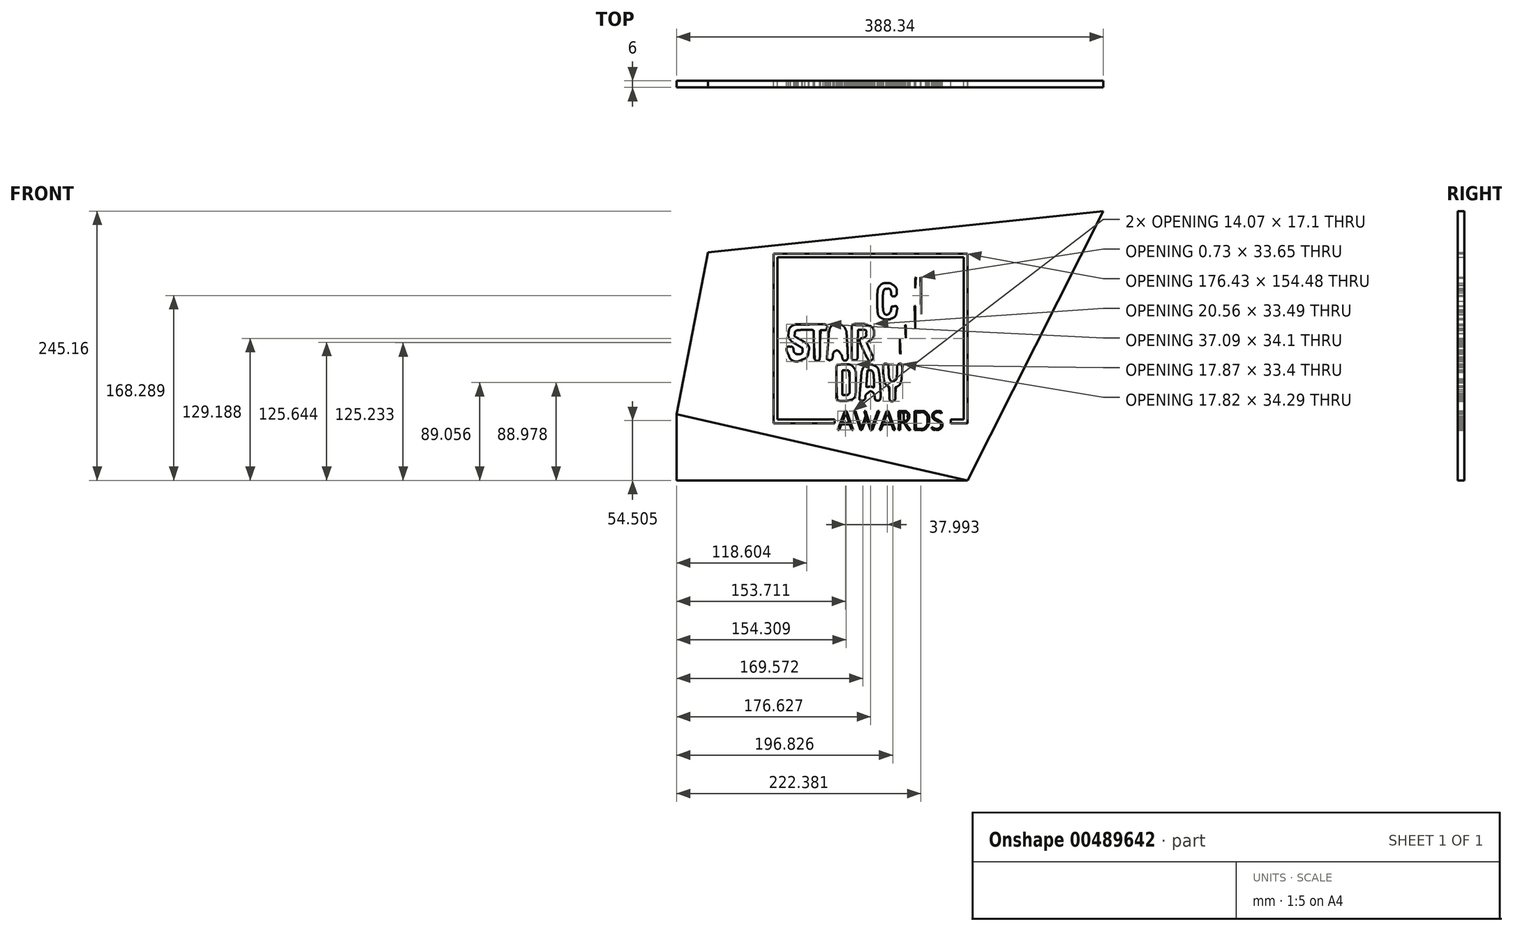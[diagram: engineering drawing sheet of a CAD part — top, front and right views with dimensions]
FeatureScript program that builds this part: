
annotation { "Feature Type Name" : "Feature", "Feature Type Description" : "" }
export const myFeature = defineFeature(function(context is Context, id is Id, definition is map)
    precondition{}
    {
        {
            var Q0;
            Q0=qCreatedBy(makeId("Front.planeOp"),FACE);
            var sketch = newSketch(context, id + "F0", { "sketchPlane" : qUnion([Q0])});
            skLineSegment(sketch, "E0", {"start": v(194.17, 122.58) * mm, "end": v(-165.67, 84.87) * mm});
            skLineSegment(sketch, "E1", {"start": v(-165.67, 84.87) * mm, "end": v(-194.17, -62.37) * mm});
            skLineSegment(sketch, "E2", {"start": v(-194.17, -62.37) * mm, "end": v(70.56, -122.58) * mm});
            skLineSegment(sketch, "E3", {"start": v(70.56, -122.58) * mm, "end": v(194.17, 122.58) * mm});
            skFitSpline(sketch, "E4", {"points": [v(25.61, 63.48) * mm, v(26.39, 63.52) * mm, v(27.2, 63.2) * mm, v(27.85, 62.53) * mm]});
            skLineSegment(sketch, "E5", {"start": v(-105.76, 83.85) * mm, "end": v(70.67, 83.85) * mm});
            skLineSegment(sketch, "E6", {"start": v(70.67, 83.85) * mm, "end": v(70.67, -70.63) * mm});
            skLineSegment(sketch, "E7", {"start": v(70.67, -70.63) * mm, "end": v(55.35, -70.63) * mm});
            skLineSegment(sketch, "E8", {"start": v(55.35, -70.63) * mm, "end": v(55.35, -67.25) * mm});
            skLineSegment(sketch, "E9", {"start": v(55.35, -67.25) * mm, "end": v(67.29, -67.25) * mm});
            skLineSegment(sketch, "E10", {"start": v(67.29, -67.25) * mm, "end": v(67.29, 80.46) * mm});
            skLineSegment(sketch, "E11", {"start": v(67.29, 80.46) * mm, "end": v(-102.37, 80.46) * mm});
            skLineSegment(sketch, "E12", {"start": v(-102.37, 80.46) * mm, "end": v(-102.37, -67.25) * mm});
            skLineSegment(sketch, "E13", {"start": v(-102.37, -67.25) * mm, "end": v(-50.2, -67.25) * mm});
            skLineSegment(sketch, "E14", {"start": v(-50.2, -67.25) * mm, "end": v(-50.2, -70.63) * mm});
            skLineSegment(sketch, "E15", {"start": v(-50.2, -70.63) * mm, "end": v(-105.76, -70.63) * mm});
            skLineSegment(sketch, "E16", {"start": v(-105.76, -70.63) * mm, "end": v(-105.76, 82.16) * mm});
            skLineSegment(sketch, "E17", {"start": v(-105.76, 82.16) * mm, "end": v(-105.76, 83.85) * mm});
            skFitSpline(sketch, "E18", {"points": [v(28.58, 28.89) * mm, v(28.61, 7.58) * mm, v(28.55, -4.5) * mm, v(28.4, -5.32) * mm]});
            skFitSpline(sketch, "E19", {"points": [v(28.4, -5.32) * mm, v(27.66, -9.33) * mm, v(24.53, -12.47) * mm, v(20.51, -13.23) * mm]});
            skLineSegment(sketch, "E20", {"start": v(27.85, 62.53) * mm, "end": v(28.52, 61.83) * mm});
            skLineSegment(sketch, "E21", {"start": v(28.52, 61.83) * mm, "end": v(28.58, 28.89) * mm});
            skLineSegment(sketch, "E22", {"start": v(28.58, 28.89) * mm, "end": v(27.85, 62.53) * mm});
            skFitSpline(sketch, "E23", {"points": [v(20.51, -13.23) * mm, v(16.18, -14.05) * mm, v(11.76, -11.73) * mm, v(9.83, -7.6) * mm]});
            skLineSegment(sketch, "E24", {"start": v(20.51, -13.23) * mm, "end": v(20.51, -13.23) * mm});
            skFitSpline(sketch, "E25", {"points": [v(8.98, 5.9) * mm, v(8.91, 19.23) * mm, v(8.87, 18.91) * mm, v(10.63, 19.77) * mm]});
            skFitSpline(sketch, "E26", {"points": [v(10.63, 19.77) * mm, v(11.38, 20.14) * mm, v(11.66, 20.16) * mm, v(12.39, 19.95) * mm]});
            skFitSpline(sketch, "E27", {"points": [v(12.39, 19.95) * mm, v(12.86, 19.8) * mm, v(13.5, 19.42) * mm, v(13.81, 19.09) * mm]});
            skLineSegment(sketch, "E28", {"start": v(9.83, -7.6) * mm, "end": v(9.05, -5.93) * mm});
            skLineSegment(sketch, "E29", {"start": v(9.05, -5.93) * mm, "end": v(8.98, 5.9) * mm});
            skLineSegment(sketch, "E30", {"start": v(8.98, 5.9) * mm, "end": v(9.83, -7.6) * mm});
            skFitSpline(sketch, "E31", {"points": [v(14.5, 6.86) * mm, v(14.62, -6.1) * mm, v(14.56, -5.6) * mm, v(16.25, -6.88) * mm]});
            skFitSpline(sketch, "E32", {"points": [v(16.25, -6.88) * mm, v(17.12, -7.55) * mm, v(18.97, -7.87) * mm, v(20.17, -7.57) * mm]});
            skFitSpline(sketch, "E33", {"points": [v(20.17, -7.57) * mm, v(21.1, -7.34) * mm, v(22.57, -5.87) * mm, v(22.83, -4.92) * mm]});
            skFitSpline(sketch, "E34", {"points": [v(22.83, -4.92) * mm, v(22.98, -4.38) * mm, v(23.07, 3.16) * mm, v(23.07, 16.04) * mm]});
            skLineSegment(sketch, "E35", {"start": v(13.81, 19.09) * mm, "end": v(14.38, 18.49) * mm});
            skLineSegment(sketch, "E36", {"start": v(14.38, 18.49) * mm, "end": v(14.5, 6.86) * mm});
            skLineSegment(sketch, "E37", {"start": v(14.5, 6.86) * mm, "end": v(13.81, 19.09) * mm});
            skFitSpline(sketch, "E38", {"points": [v(22.47, 36.37) * mm, v(21.71, 36.66) * mm, v(15.42, 36.66) * mm, v(14.96, 36.37) * mm]});
            skFitSpline(sketch, "E39", {"points": [v(14.96, 36.37) * mm, v(14.67, 36.2) * mm, v(14.59, 35.18) * mm, v(14.5, 30.49) * mm]});
            skFitSpline(sketch, "E40", {"points": [v(14.5, 30.49) * mm, v(14.38, 24.9) * mm, v(14.37, 24.8) * mm, v(13.82, 24.23) * mm]});
            skFitSpline(sketch, "E41", {"points": [v(13.82, 24.23) * mm, v(13, 23.36) * mm, v(11.98, 23.08) * mm, v(10.9, 23.44) * mm]});
            skFitSpline(sketch, "E42", {"points": [v(10.9, 23.44) * mm, v(9.08, 24.05) * mm, v(9.19, 23.16) * mm, v(9.01, 39.2) * mm]});
            skFitSpline(sketch, "E43", {"points": [v(9.01, 39.2) * mm, v(8.87, 52.48) * mm, v(8.88, 53.56) * mm, v(9.26, 54.55) * mm]});
            skFitSpline(sketch, "E44", {"points": [v(9.26, 54.55) * mm, v(9.72, 55.74) * mm, v(10.52, 56.3) * mm, v(11.76, 56.3) * mm]});
            skFitSpline(sketch, "E45", {"points": [v(11.76, 56.3) * mm, v(12.76, 56.3) * mm, v(13.89, 55.6) * mm, v(14.21, 54.76) * mm]});
            skFitSpline(sketch, "E46", {"points": [v(14.21, 54.76) * mm, v(14.36, 54.38) * mm, v(14.55, 51.58) * mm, v(14.66, 48.19) * mm]});
            skLineSegment(sketch, "E47", {"start": v(23.07, 16.04) * mm, "end": v(23.07, 36.15) * mm});
            skLineSegment(sketch, "E48", {"start": v(23.07, 36.15) * mm, "end": v(22.47, 36.37) * mm});
            skLineSegment(sketch, "E49", {"start": v(22.47, 36.37) * mm, "end": v(23.07, 16.04) * mm});
            skFitSpline(sketch, "E50", {"points": [v(18.71, 42.22) * mm, v(22.24, 42.16) * mm, v(22.6, 42.19) * mm, v(22.8, 42.57) * mm]});
            skFitSpline(sketch, "E51", {"points": [v(22.8, 42.57) * mm, v(22.94, 42.81) * mm, v(23.03, 46.77) * mm, v(23.03, 52.21) * mm]});
            skLineSegment(sketch, "E52", {"start": v(14.66, 48.19) * mm, "end": v(14.84, 42.28) * mm});
            skLineSegment(sketch, "E53", {"start": v(14.84, 42.28) * mm, "end": v(18.71, 42.22) * mm});
            skLineSegment(sketch, "E54", {"start": v(18.71, 42.22) * mm, "end": v(14.66, 48.19) * mm});
            skFitSpline(sketch, "E55", {"points": [v(23.63, 62.34) * mm, v(24.1, 63.06) * mm, v(24.84, 63.45) * mm, v(25.61, 63.48) * mm]});
            skLineSegment(sketch, "E56", {"start": v(23.03, 52.21) * mm, "end": v(23.04, 61.44) * mm});
            skLineSegment(sketch, "E57", {"start": v(23.04, 61.44) * mm, "end": v(23.63, 62.34) * mm});
            skLineSegment(sketch, "E58", {"start": v(23.63, 62.34) * mm, "end": v(23.03, 52.21) * mm});
            skLineSegment(sketch, "E59", {"start": v(25.61, 63.48) * mm, "end": v(25.61, 63.48) * mm});
            skFitSpline(sketch, "E60", {"points": [v(-44, 57.23) * mm, v(-34.34, 57.23) * mm, v(-34.33, 57.23) * mm, v(-33.6, 55.7) * mm]});
            skFitSpline(sketch, "E61", {"points": [v(-33.6, 55.7) * mm, v(-33.16, 54.77) * mm, v(-33.16, 54.41) * mm, v(-33.59, 53.39) * mm]});
            skFitSpline(sketch, "E62", {"points": [v(-33.59, 53.39) * mm, v(-34.12, 52.11) * mm, v(-35.35, 51.68) * mm, v(-38.4, 51.67) * mm]});
            skFitSpline(sketch, "E63", {"points": [v(-38.4, 51.67) * mm, v(-40.52, 51.67) * mm, v(-40.91, 51.6) * mm, v(-41.1, 51.26) * mm]});
            skFitSpline(sketch, "E64", {"points": [v(-41.1, 51.26) * mm, v(-41.22, 51.03) * mm, v(-41.32, 45.5) * mm, v(-41.33, 38.48) * mm]});
            skFitSpline(sketch, "E65", {"points": [v(-41.33, 38.48) * mm, v(-41.35, 25.1) * mm, v(-41.3, 25.51) * mm, v(-42.6, 24.67) * mm]});
            skFitSpline(sketch, "E66", {"points": [v(-42.6, 24.67) * mm, v(-43.45, 24.11) * mm, v(-44.41, 24.04) * mm, v(-45.26, 24.47) * mm]});
            skFitSpline(sketch, "E67", {"points": [v(-45.26, 24.47) * mm, v(-46.87, 25.28) * mm, v(-46.8, 24.7) * mm, v(-46.86, 38.33) * mm]});
            skFitSpline(sketch, "E68", {"points": [v(-46.86, 38.33) * mm, v(-46.9, 45.09) * mm, v(-46.98, 50.86) * mm, v(-47.04, 51.14) * mm]});
            skFitSpline(sketch, "E69", {"points": [v(-47.04, 51.14) * mm, v(-47.16, 51.64) * mm, v(-47.27, 51.67) * mm, v(-49.49, 51.67) * mm]});
            skFitSpline(sketch, "E70", {"points": [v(-49.49, 51.67) * mm, v(-52.1, 51.67) * mm, v(-53.06, 51.95) * mm, v(-53.86, 52.97) * mm]});
            skFitSpline(sketch, "E71", {"points": [v(-53.86, 52.97) * mm, v(-54.64, 53.96) * mm, v(-54.44, 55.68) * mm, v(-53.44, 56.58) * mm]});
            skLineSegment(sketch, "E72", {"start": v(-52.71, 57.23) * mm, "end": v(-44, 57.23) * mm});
            skLineSegment(sketch, "E73", {"start": v(-44, 57.23) * mm, "end": v(-52.71, 57.23) * mm});
            skFitSpline(sketch, "E74", {"points": [v(-21.12, 57.18) * mm, v(-18.97, 57.2) * mm, v(-17.15, 57.15) * mm, v(-16.73, 57.01) * mm]});
            skFitSpline(sketch, "E75", {"points": [v(-16.73, 57.01) * mm, v(-14.36, 56.23) * mm, v(-13.97, 53.27) * mm, v(-16.08, 52.04) * mm]});
            skFitSpline(sketch, "E76", {"points": [v(-16.08, 52.04) * mm, v(-16.78, 51.63) * mm, v(-17.34, 51.57) * mm, v(-20.9, 51.54) * mm]});
            skFitSpline(sketch, "E77", {"points": [v(-20.9, 51.54) * mm, v(-23.12, 51.51) * mm, v(-25.03, 51.4) * mm, v(-25.14, 51.3) * mm]});
            skFitSpline(sketch, "E78", {"points": [v(-25.14, 51.3) * mm, v(-25.47, 50.96) * mm, v(-25.49, 44.97) * mm, v(-25.16, 44.64) * mm]});
            skFitSpline(sketch, "E79", {"points": [v(-25.16, 44.64) * mm, v(-24.92, 44.4) * mm, v(-21.76, 44.25) * mm, v(-17.06, 44.25) * mm]});
            skFitSpline(sketch, "E80", {"points": [v(-17.06, 44.25) * mm, v(-16.48, 44.25) * mm, v(-16.08, 44.04) * mm, v(-15.47, 43.43) * mm]});
            skFitSpline(sketch, "E81", {"points": [v(-15.47, 43.43) * mm, v(-14.7, 42.67) * mm, v(-14.66, 42.54) * mm, v(-14.76, 41.44) * mm]});
            skFitSpline(sketch, "E82", {"points": [v(-14.76, 41.44) * mm, v(-14.9, 40.03) * mm, v(-15.6, 39.22) * mm, v(-16.93, 38.9) * mm]});
            skFitSpline(sketch, "E83", {"points": [v(-16.93, 38.9) * mm, v(-17.43, 38.8) * mm, v(-19.48, 38.7) * mm, v(-21.5, 38.7) * mm]});
            skFitSpline(sketch, "E84", {"points": [v(-21.5, 38.7) * mm, v(-24.76, 38.69) * mm, v(-25.17, 38.64) * mm, v(-25.31, 38.28) * mm]});
            skFitSpline(sketch, "E85", {"points": [v(-25.31, 38.28) * mm, v(-25.52, 37.75) * mm, v(-25.53, 30.58) * mm, v(-25.32, 30.05) * mm]});
            skFitSpline(sketch, "E86", {"points": [v(-25.32, 30.05) * mm, v(-25.17, 29.69) * mm, v(-24.75, 29.65) * mm, v(-21.2, 29.65) * mm]});
            skFitSpline(sketch, "E87", {"points": [v(-21.2, 29.65) * mm, v(-16.85, 29.65) * mm, v(-16.09, 29.48) * mm, v(-15.19, 28.34) * mm]});
            skFitSpline(sketch, "E88", {"points": [v(-15.19, 28.34) * mm, v(-14.76, 27.8) * mm, v(-14.68, 27.47) * mm, v(-14.77, 26.56) * mm]});
            skFitSpline(sketch, "E89", {"points": [v(-14.77, 26.56) * mm, v(-14.93, 24.88) * mm, v(-15.6, 24.32) * mm, v(-17.75, 24.07) * mm]});
            skFitSpline(sketch, "E90", {"points": [v(-17.75, 24.07) * mm, v(-19.9, 23.82) * mm, v(-27.76, 23.84) * mm, v(-28.84, 24.1) * mm]});
            skFitSpline(sketch, "E91", {"points": [v(-28.84, 24.1) * mm, v(-30.04, 24.37) * mm, v(-30.86, 25.42) * mm, v(-31.04, 26.9) * mm]});
            skFitSpline(sketch, "E92", {"points": [v(-31.04, 26.9) * mm, v(-31.13, 27.59) * mm, v(-31.16, 34.2) * mm, v(-31.12, 41.58) * mm]});
            skFitSpline(sketch, "E93", {"points": [v(-31.12, 41.58) * mm, v(-31.04, 56.16) * mm, v(-31.05, 56.08) * mm, v(-29.77, 56.69) * mm]});
            skFitSpline(sketch, "E94", {"points": [v(-29.77, 56.69) * mm, v(-29.22, 56.95) * mm, v(-24.7, 57.16) * mm, v(-21.12, 57.18) * mm]});
            skLineSegment(sketch, "E95", {"start": v(-53.44, 56.58) * mm, "end": v(-52.71, 57.23) * mm});
            skLineSegment(sketch, "E96", {"start": v(-52.71, 57.23) * mm, "end": v(-53.44, 56.58) * mm});
            skFitSpline(sketch, "E97", {"points": [v(-2.88, 57) * mm, v(-0.9, 57.04) * mm, v(1.1, 56.52) * mm, v(2.56, 55.42) * mm]});
            skFitSpline(sketch, "E98", {"points": [v(2.56, 55.42) * mm, v(4.95, 53.61) * mm, v(6.15, 51.23) * mm, v(6.15, 48.3) * mm]});
            skFitSpline(sketch, "E99", {"points": [v(6.15, 48.3) * mm, v(6.15, 46.72) * mm, v(6.1, 46.5) * mm, v(5.47, 45.82) * mm]});
            skFitSpline(sketch, "E100", {"points": [v(5.47, 45.82) * mm, v(4.9, 45.17) * mm, v(4.64, 45.06) * mm, v(3.74, 45.06) * mm]});
            skFitSpline(sketch, "E101", {"points": [v(3.74, 45.06) * mm, v(2.2, 45.06) * mm, v(1.39, 45.94) * mm, v(1.07, 47.92) * mm]});
            skFitSpline(sketch, "E102", {"points": [v(1.07, 47.92) * mm, v(0.65, 50.58) * mm, v(-0.54, 51.76) * mm, v(-2.79, 51.76) * mm]});
            skFitSpline(sketch, "E103", {"points": [v(-2.79, 51.76) * mm, v(-4.16, 51.76) * mm, v(-5.02, 51.3) * mm, v(-5.55, 50.28) * mm]});
            skFitSpline(sketch, "E104", {"points": [v(-5.55, 50.28) * mm, v(-6.08, 49.26) * mm, v(-6.36, 45.87) * mm, v(-6.36, 40.54) * mm]});
            skFitSpline(sketch, "E105", {"points": [v(-6.36, 40.54) * mm, v(-6.35, 35.14) * mm, v(-6.07, 31.58) * mm, v(-5.57, 30.6) * mm]});
            skFitSpline(sketch, "E106", {"points": [v(-5.57, 30.6) * mm, v(-4.55, 28.64) * mm, v(-1.68, 28.5) * mm, v(0, 30.35) * mm]});
            skFitSpline(sketch, "E107", {"points": [v(0, 30.35) * mm, v(0.62, 31.05) * mm, v(0.82, 31.54) * mm, v(1.05, 32.88) * mm]});
            skFitSpline(sketch, "E108", {"points": [v(1.05, 32.88) * mm, v(1.4, 35) * mm, v(1.95, 35.68) * mm, v(3.38, 35.83) * mm]});
            skFitSpline(sketch, "E109", {"points": [v(3.38, 35.83) * mm, v(5.61, 36.05) * mm, v(6.67, 34.44) * mm, v(6.19, 31.53) * mm]});
            skFitSpline(sketch, "E110", {"points": [v(6.19, 31.53) * mm, v(5.68, 28.48) * mm, v(3.82, 25.95) * mm, v(1.17, 24.69) * mm]});
            skFitSpline(sketch, "E111", {"points": [v(1.17, 24.69) * mm, v(0.05, 24.16) * mm, v(-0.61, 24.01) * mm, v(-2.2, 23.95) * mm]});
            skFitSpline(sketch, "E112", {"points": [v(-2.2, 23.95) * mm, v(-4.4, 23.86) * mm, v(-5.4, 24.05) * mm, v(-7, 24.87) * mm]});
            skFitSpline(sketch, "E113", {"points": [v(-7, 24.87) * mm, v(-9, 25.9) * mm, v(-10.82, 28.38) * mm, v(-11.11, 30.5) * mm]});
            skFitSpline(sketch, "E114", {"points": [v(-11.11, 30.5) * mm, v(-11.34, 32.1) * mm, v(-11.4, 48.03) * mm, v(-11.2, 49.58) * mm]});
            skFitSpline(sketch, "E115", {"points": [v(-11.2, 49.58) * mm, v(-10.93, 51.47) * mm, v(-9.93, 53.65) * mm, v(-8.8, 54.79) * mm]});
            skFitSpline(sketch, "E116", {"points": [v(-8.8, 54.79) * mm, v(-7.37, 56.21) * mm, v(-5.13, 56.97) * mm, v(-2.88, 57) * mm]});
            skLineSegment(sketch, "E117", {"start": v(-21.12, 57.18) * mm, "end": v(-21.12, 57.18) * mm});
            skFitSpline(sketch, "E118", {"points": [v(-4.3, 20.06) * mm, v(0.03, 20.07) * mm, v(4.36, 19.96) * mm, v(4.8, 19.72) * mm]});
            skFitSpline(sketch, "E119", {"points": [v(4.8, 19.72) * mm, v(6, 19.08) * mm, v(6.5, 17.24) * mm, v(5.87, 15.85) * mm]});
            skFitSpline(sketch, "E120", {"points": [v(5.87, 15.85) * mm, v(5.4, 14.81) * mm, v(4.46, 14.5) * mm, v(1.4, 14.4) * mm]});
            skFitSpline(sketch, "E121", {"points": [v(1.4, 14.4) * mm, v(-0.3, 14.33) * mm, v(-1.45, 14.2) * mm, v(-1.55, 14.03) * mm]});
            skFitSpline(sketch, "E122", {"points": [v(-1.55, 14.03) * mm, v(-1.65, 13.89) * mm, v(-1.72, 8.21) * mm, v(-1.73, 1.42) * mm]});
            skFitSpline(sketch, "E123", {"points": [v(-1.73, 1.42) * mm, v(-1.73, -11.88) * mm, v(-1.72, -11.78) * mm, v(-2.94, -12.63) * mm]});
            skFitSpline(sketch, "E124", {"points": [v(-2.94, -12.63) * mm, v(-3.73, -13.19) * mm, v(-5.43, -13.1) * mm, v(-6.17, -12.47) * mm]});
            skFitSpline(sketch, "E125", {"points": [v(-6.17, -12.47) * mm, v(-6.5, -12.19) * mm, v(-6.9, -11.73) * mm, v(-7.04, -11.45) * mm]});
            skFitSpline(sketch, "E126", {"points": [v(-7.04, -11.45) * mm, v(-7.21, -11.1) * mm, v(-7.3, -7.02) * mm, v(-7.3, 1.6) * mm]});
            skFitSpline(sketch, "E127", {"points": [v(-7.3, 1.6) * mm, v(-7.3, 12.68) * mm, v(-7.33, 14.15) * mm, v(-7.65, 14.27) * mm]});
            skFitSpline(sketch, "E128", {"points": [v(-7.65, 14.27) * mm, v(-7.85, 14.35) * mm, v(-8.76, 14.43) * mm, v(-9.68, 14.46) * mm]});
            skFitSpline(sketch, "E129", {"points": [v(-9.68, 14.46) * mm, v(-13.17, 14.56) * mm, v(-13.09, 14.54) * mm, v(-13.92, 15.37) * mm]});
            skFitSpline(sketch, "E130", {"points": [v(-13.92, 15.37) * mm, v(-14.56, 16.01) * mm, v(-14.7, 16.34) * mm, v(-14.7, 17.12) * mm]});
            skFitSpline(sketch, "E131", {"points": [v(-14.7, 17.12) * mm, v(-14.7, 18.32) * mm, v(-14.24, 19.25) * mm, v(-13.42, 19.69) * mm]});
            skFitSpline(sketch, "E132", {"points": [v(-13.42, 19.69) * mm, v(-12.97, 19.93) * mm, v(-8.64, 20.06) * mm, v(-4.3, 20.06) * mm]});
            skFitSpline(sketch, "E133", {"points": [v(-28.16, 19.77) * mm, v(-23.87, 19.8) * mm, v(-22.59, 19.59) * mm, v(-20.44, 18.5) * mm]});
            skFitSpline(sketch, "E134", {"points": [v(-20.44, 18.5) * mm, v(-15.48, 15.96) * mm, v(-14.92, 8.12) * mm, v(-19.4, 4.02) * mm]});
            skFitSpline(sketch, "E135", {"points": [v(-19.4, 4.02) * mm, v(-20.08, 3.4) * mm, v(-20.72, 2.75) * mm, v(-20.8, 2.6) * mm]});
            skFitSpline(sketch, "E136", {"points": [v(-20.8, 2.6) * mm, v(-20.9, 2.44) * mm, v(-20.16, 0.53) * mm, v(-19.09, -1.8) * mm]});
            skFitSpline(sketch, "E137", {"points": [v(-19.09, -1.8) * mm, v(-18.05, -4.07) * mm, v(-16.8, -6.8) * mm, v(-16.3, -7.87) * mm]});
            skFitSpline(sketch, "E138", {"points": [v(-16.3, -7.87) * mm, v(-15.2, -10.26) * mm, v(-15.14, -11.3) * mm, v(-16.04, -12.3) * mm]});
            skFitSpline(sketch, "E139", {"points": [v(-16.04, -12.3) * mm, v(-17.13, -13.51) * mm, v(-19.33, -13.36) * mm, v(-20.07, -12.03) * mm]});
            skFitSpline(sketch, "E140", {"points": [v(-20.07, -12.03) * mm, v(-22, -8.55) * mm, v(-27.46, 3.74) * mm, v(-27.46, 4.6) * mm]});
            skFitSpline(sketch, "E141", {"points": [v(-27.46, 4.6) * mm, v(-27.46, 5.65) * mm, v(-26.47, 6.64) * mm, v(-25, 7.07) * mm]});
            skFitSpline(sketch, "E142", {"points": [v(-25, 7.07) * mm, v(-22.8, 7.7) * mm, v(-21.66, 9.12) * mm, v(-21.66, 11.21) * mm]});
            skFitSpline(sketch, "E143", {"points": [v(-21.66, 11.21) * mm, v(-21.66, 13.68) * mm, v(-22.82, 14.44) * mm, v(-26.64, 14.46) * mm]});
            skFitSpline(sketch, "E144", {"points": [v(-29.3, 1.6) * mm, v(-29.4, -8.12) * mm, v(-29.5, -11.38) * mm, v(-29.72, -11.77) * mm]});
            skFitSpline(sketch, "E145", {"points": [v(-29.72, -11.77) * mm, v(-30.2, -12.6) * mm, v(-30.96, -13) * mm, v(-32.12, -13) * mm]});
            skFitSpline(sketch, "E146", {"points": [v(-32.12, -13) * mm, v(-33.64, -13) * mm, v(-34.55, -12.1) * mm, v(-34.75, -10.39) * mm]});
            skFitSpline(sketch, "E147", {"points": [v(-34.75, -10.39) * mm, v(-34.83, -9.72) * mm, v(-34.87, -3.12) * mm, v(-34.83, 4.28) * mm]});
            skFitSpline(sketch, "E148", {"points": [v(-34.83, 4.28) * mm, v(-34.76, 16.85) * mm, v(-34.73, 17.78) * mm, v(-34.33, 18.38) * mm]});
            skFitSpline(sketch, "E149", {"points": [v(-34.33, 18.38) * mm, v(-33.59, 19.52) * mm, v(-32.64, 19.73) * mm, v(-28.16, 19.77) * mm]});
            skLineSegment(sketch, "E150", {"start": v(-26.64, 14.46) * mm, "end": v(-29.2, 14.47) * mm});
            skLineSegment(sketch, "E151", {"start": v(-29.2, 14.47) * mm, "end": v(-29.3, 1.6) * mm});
            skLineSegment(sketch, "E152", {"start": v(-29.3, 1.6) * mm, "end": v(-26.64, 14.46) * mm});
            skFitSpline(sketch, "E153", {"points": [v(-58.5, 19.16) * mm, v(-57.44, 18.45) * mm, v(-57.02, 17.24) * mm, v(-57.42, 16.05) * mm]});
            skFitSpline(sketch, "E154", {"points": [v(-57.42, 16.05) * mm, v(-57.86, 14.72) * mm, v(-58.7, 14.26) * mm, v(-60.78, 14.17) * mm]});
            skFitSpline(sketch, "E155", {"points": [v(-60.78, 14.17) * mm, v(-61.76, 14.13) * mm, v(-62.8, 14.05) * mm, v(-63.09, 13.99) * mm]});
            skLineSegment(sketch, "E156", {"start": v(-59.3, 19.7) * mm, "end": v(-58.5, 19.16) * mm});
            skLineSegment(sketch, "E157", {"start": v(-58.5, 19.16) * mm, "end": v(-59.3, 19.7) * mm});
            skFitSpline(sketch, "E158", {"points": [v(-63.62, 2) * mm, v(-63.62, -4.53) * mm, v(-63.72, -10.29) * mm, v(-63.84, -10.8) * mm]});
            skFitSpline(sketch, "E159", {"points": [v(-63.84, -10.8) * mm, v(-64.32, -12.91) * mm, v(-66.72, -13.73) * mm, v(-68.3, -12.32) * mm]});
            skLineSegment(sketch, "E160", {"start": v(-63.09, 13.99) * mm, "end": v(-63.61, 13.88) * mm});
            skLineSegment(sketch, "E161", {"start": v(-63.61, 13.88) * mm, "end": v(-63.62, 2) * mm});
            skLineSegment(sketch, "E162", {"start": v(-63.62, 2) * mm, "end": v(-63.09, 13.99) * mm});
            skFitSpline(sketch, "E163", {"points": [v(-69.17, 1.01) * mm, v(-69.27, 11.93) * mm, v(-69.34, 13.7) * mm, v(-69.64, 13.9) * mm]});
            skFitSpline(sketch, "E164", {"points": [v(-69.64, 13.9) * mm, v(-70.17, 14.23) * mm, v(-83.7, 14.16) * mm, v(-84.68, 13.82) * mm]});
            skFitSpline(sketch, "E165", {"points": [v(-84.68, 13.82) * mm, v(-85.75, 13.44) * mm, v(-86.37, 12.53) * mm, v(-86.5, 11.13) * mm]});
            skFitSpline(sketch, "E166", {"points": [v(-86.5, 11.13) * mm, v(-86.72, 8.88) * mm, v(-86.13, 8.22) * mm, v(-81.43, 5.53) * mm]});
            skFitSpline(sketch, "E167", {"points": [v(-81.43, 5.53) * mm, v(-79.85, 4.63) * mm, v(-78, 3.47) * mm, v(-77.32, 2.95) * mm]});
            skFitSpline(sketch, "E168", {"points": [v(-77.32, 2.95) * mm, v(-74.75, 1.01) * mm, v(-73.5, -2.07) * mm, v(-74.04, -5.13) * mm]});
            skFitSpline(sketch, "E169", {"points": [v(-74.04, -5.13) * mm, v(-74.7, -8.8) * mm, v(-76.87, -11.5) * mm, v(-80.07, -12.67) * mm]});
            skFitSpline(sketch, "E170", {"points": [v(-80.07, -12.67) * mm, v(-84.92, -14.42) * mm, v(-90.27, -12.3) * mm, v(-92.39, -7.77) * mm]});
            skFitSpline(sketch, "E171", {"points": [v(-92.39, -7.77) * mm, v(-94.1, -4.11) * mm, v(-93.27, -0.94) * mm, v(-90.6, -0.94) * mm]});
            skFitSpline(sketch, "E172", {"points": [v(-90.6, -0.94) * mm, v(-88.9, -0.94) * mm, v(-88.03, -1.98) * mm, v(-87.6, -4.5) * mm]});
            skFitSpline(sketch, "E173", {"points": [v(-87.6, -4.5) * mm, v(-87.43, -5.52) * mm, v(-86.2, -7) * mm, v(-85.16, -7.44) * mm]});
            skFitSpline(sketch, "E174", {"points": [v(-85.16, -7.44) * mm, v(-84.76, -7.6) * mm, v(-83.93, -7.68) * mm, v(-83.21, -7.62) * mm]});
            skFitSpline(sketch, "E175", {"points": [v(-83.21, -7.62) * mm, v(-81.04, -7.44) * mm, v(-79.6, -5.9) * mm, v(-79.6, -3.75) * mm]});
            skFitSpline(sketch, "E176", {"points": [v(-79.6, -3.75) * mm, v(-79.6, -2.42) * mm, v(-80.37, -1.66) * mm, v(-83.63, 0.26) * mm]});
            skFitSpline(sketch, "E177", {"points": [v(-83.63, 0.26) * mm, v(-87.4, 2.47) * mm, v(-89.66, 4.04) * mm, v(-90.33, 4.93) * mm]});
            skFitSpline(sketch, "E178", {"points": [v(-90.33, 4.93) * mm, v(-91.71, 6.74) * mm, v(-92.47, 9.23) * mm, v(-92.22, 11.1) * mm]});
            skFitSpline(sketch, "E179", {"points": [v(-92.22, 11.1) * mm, v(-91.68, 15) * mm, v(-89.99, 17.58) * mm, v(-87.05, 18.96) * mm]});
            skLineSegment(sketch, "E180", {"start": v(-68.3, -12.32) * mm, "end": v(-69.06, -11.64) * mm});
            skLineSegment(sketch, "E181", {"start": v(-69.06, -11.64) * mm, "end": v(-69.17, 1.01) * mm});
            skLineSegment(sketch, "E182", {"start": v(-69.17, 1.01) * mm, "end": v(-68.3, -12.32) * mm});
            skFitSpline(sketch, "E183", {"points": [v(38.27, 19.68) * mm, v(42.97, 19.68) * mm, v(43.83, 19.62) * mm, v(45.13, 19.22) * mm]});
            skFitSpline(sketch, "E184", {"points": [v(45.13, 19.22) * mm, v(51.98, 17.1) * mm, v(54.28, 8.86) * mm, v(49.48, 3.6) * mm]});
            skFitSpline(sketch, "E185", {"points": [v(49.48, 3.6) * mm, v(47.42, 1.35) * mm, v(45.1, 0.45) * mm, v(41.3, 0.45) * mm]});
            skFitSpline(sketch, "E186", {"points": [v(41.3, 0.45) * mm, v(39.93, 0.45) * mm, v(38.6, 0.34) * mm, v(38.35, 0.2) * mm]});
            skFitSpline(sketch, "E187", {"points": [v(38.35, 0.2) * mm, v(37.93, -0.02) * mm, v(37.9, -0.33) * mm, v(37.9, -5.38) * mm]});
            skFitSpline(sketch, "E188", {"points": [v(37.9, -5.38) * mm, v(37.9, -11.1) * mm, v(37.77, -11.88) * mm, v(36.66, -12.66) * mm]});
            skFitSpline(sketch, "E189", {"points": [v(36.66, -12.66) * mm, v(36, -13.12) * mm, v(34.2, -13.08) * mm, v(33.57, -12.59) * mm]});
            skFitSpline(sketch, "E190", {"points": [v(33.57, -12.59) * mm, v(32.34, -11.63) * mm, v(32.34, -11.64) * mm, v(32.34, 4.33) * mm]});
            skFitSpline(sketch, "E191", {"points": [v(32.34, 4.33) * mm, v(32.34, 15.53) * mm, v(32.4, 19.2) * mm, v(32.62, 19.4) * mm]});
            skFitSpline(sketch, "E192", {"points": [v(32.62, 19.4) * mm, v(32.82, 19.6) * mm, v(34.4, 19.68) * mm, v(38.27, 19.68) * mm]});
            skLineSegment(sketch, "E193", {"start": v(-87.05, 18.96) * mm, "end": v(-85.74, 19.57) * mm});
            skLineSegment(sketch, "E194", {"start": v(-85.74, 19.57) * mm, "end": v(-72.53, 19.63) * mm});
            skLineSegment(sketch, "E195", {"start": v(-72.53, 19.63) * mm, "end": v(-59.3, 19.7) * mm});
            skLineSegment(sketch, "E196", {"start": v(-59.3, 19.7) * mm, "end": v(-87.05, 18.96) * mm});
            skFitSpline(sketch, "E197", {"points": [v(-47.75, 19.59) * mm, v(-46.55, 19.6) * mm, v(-45.35, 19.42) * mm, v(-44.56, 19.05) * mm]});
            skFitSpline(sketch, "E198", {"points": [v(-44.56, 19.05) * mm, v(-42.93, 18.31) * mm, v(-41.23, 16.6) * mm, v(-40.41, 14.88) * mm]});
            skFitSpline(sketch, "E199", {"points": [v(-40.41, 14.88) * mm, v(-39.56, 13.1) * mm, v(-39.47, 12.25) * mm, v(-38.81, 0.62) * mm]});
            skFitSpline(sketch, "E200", {"points": [v(-38.81, 0.62) * mm, v(-38.2, -10.18) * mm, v(-38.2, -11.37) * mm, v(-38.82, -12.15) * mm]});
            skFitSpline(sketch, "E201", {"points": [v(-38.82, -12.15) * mm, v(-39.75, -13.33) * mm, v(-42.11, -13.38) * mm, v(-42.86, -12.23) * mm]});
            skFitSpline(sketch, "E202", {"points": [v(-42.86, -12.23) * mm, v(-43.04, -11.95) * mm, v(-43.36, -10.95) * mm, v(-43.57, -10.02) * mm]});
            skFitSpline(sketch, "E203", {"points": [v(-43.57, -10.02) * mm, v(-43.9, -8.54) * mm, v(-44.1, -8.16) * mm, v(-45.04, -7.2) * mm]});
            skFitSpline(sketch, "E204", {"points": [v(-45.04, -7.2) * mm, v(-47.76, -4.39) * mm, v(-51.12, -5.7) * mm, v(-52, -9.94) * mm]});
            skFitSpline(sketch, "E205", {"points": [v(-52, -9.94) * mm, v(-52.36, -11.68) * mm, v(-52.86, -12.52) * mm, v(-53.77, -12.9) * mm]});
            skFitSpline(sketch, "E206", {"points": [v(-53.77, -12.9) * mm, v(-54.73, -13.3) * mm, v(-54.95, -13.3) * mm, v(-55.91, -12.88) * mm]});
            skFitSpline(sketch, "E207", {"points": [v(-55.91, -12.88) * mm, v(-57.36, -12.25) * mm, v(-57.42, -11.72) * mm, v(-56.9, -5.06) * mm]});
            skFitSpline(sketch, "E208", {"points": [v(-56.9, -5.06) * mm, v(-55.67, 10.46) * mm, v(-55.46, 12.7) * mm, v(-55.13, 13.89) * mm]});
            skFitSpline(sketch, "E209", {"points": [v(-55.13, 13.89) * mm, v(-54.43, 16.37) * mm, v(-53.04, 18.1) * mm, v(-50.98, 19.03) * mm]});
            skFitSpline(sketch, "E210", {"points": [v(-50.98, 19.03) * mm, v(-50.17, 19.4) * mm, v(-48.96, 19.58) * mm, v(-47.75, 19.59) * mm]});
            skFitSpline(sketch, "E211", {"points": [v(-47.88, 14.39) * mm, v(-48.67, 14.37) * mm, v(-49.41, 13.98) * mm, v(-49.81, 13.2) * mm]});
            skFitSpline(sketch, "E212", {"points": [v(-49.81, 13.2) * mm, v(-50.26, 12.35) * mm, v(-50.69, 8.24) * mm, v(-51.15, 0.45) * mm]});
            skFitSpline(sketch, "E213", {"points": [v(-51.15, 0.45) * mm, v(-51.22, -0.71) * mm, v(-51.24, -0.7) * mm, v(-48.84, -0.57) * mm]});
            skFitSpline(sketch, "E214", {"points": [v(-48.84, -0.57) * mm, v(-47.22, -0.48) * mm, v(-46.28, -0.54) * mm, v(-45.53, -0.78) * mm]});
            skFitSpline(sketch, "E215", {"points": [v(-45.53, -0.78) * mm, v(-44.71, -1.04) * mm, v(-44.44, -1.05) * mm, v(-44.26, -0.83) * mm]});
            skFitSpline(sketch, "E216", {"points": [v(-44.26, -0.83) * mm, v(-43.82, -0.3) * mm, v(-44.64, 11.68) * mm, v(-45.19, 12.74) * mm]});
            skFitSpline(sketch, "E217", {"points": [v(-45.19, 12.74) * mm, v(-45.76, 13.84) * mm, v(-46.86, 14.42) * mm, v(-47.88, 14.39) * mm]});
            skFitSpline(sketch, "E218", {"points": [v(39.95, 14.1) * mm, v(38.95, 14.1) * mm, v(38.43, 14.04) * mm, v(38.25, 13.89) * mm]});
            skFitSpline(sketch, "E219", {"points": [v(38.25, 13.89) * mm, v(37.97, 13.65) * mm, v(37.9, 12.92) * mm, v(37.9, 10.1) * mm]});
            skFitSpline(sketch, "E220", {"points": [v(37.9, 10.1) * mm, v(37.9, 8.16) * mm, v(37.99, 6.47) * mm, v(38.08, 6.32) * mm]});
            skFitSpline(sketch, "E221", {"points": [v(38.08, 6.32) * mm, v(38.17, 6.18) * mm, v(38.46, 6) * mm, v(38.71, 5.94) * mm]});
            skFitSpline(sketch, "E222", {"points": [v(38.71, 5.94) * mm, v(39.4, 5.77) * mm, v(43, 6) * mm, v(43.83, 6.25) * mm]});
            skFitSpline(sketch, "E223", {"points": [v(43.83, 6.25) * mm, v(45.16, 6.68) * mm, v(46.48, 8.6) * mm, v(46.48, 10.1) * mm]});
            skFitSpline(sketch, "E224", {"points": [v(46.48, 10.1) * mm, v(46.48, 11.16) * mm, v(45.57, 12.7) * mm, v(44.56, 13.38) * mm]});
            skFitSpline(sketch, "E225", {"points": [v(44.56, 13.38) * mm, v(43.72, 13.94) * mm, v(43.37, 14) * mm, v(41.1, 14.09) * mm]});
            skFitSpline(sketch, "E226", {"points": [v(41.1, 14.09) * mm, v(40.66, 14.1) * mm, v(40.28, 14.1) * mm, v(39.95, 14.1) * mm]});
            skFitSpline(sketch, "E227", {"points": [v(9.31, -16.4) * mm, v(9.94, -16.41) * mm, v(10.58, -16.62) * mm, v(10.98, -17.02) * mm]});
            skFitSpline(sketch, "E228", {"points": [v(11.29, -21.76) * mm, v(10.91, -27.37) * mm, v(10.37, -31.63) * mm, v(9.85, -33.13) * mm]});
            skFitSpline(sketch, "E229", {"points": [v(9.85, -33.13) * mm, v(9.15, -35.1) * mm, v(8, -36.35) * mm, v(5.7, -37.61) * mm]});
            skLineSegment(sketch, "E230", {"start": v(10.98, -17.02) * mm, "end": v(11.57, -17.62) * mm});
            skLineSegment(sketch, "E231", {"start": v(11.57, -17.62) * mm, "end": v(11.29, -21.76) * mm});
            skLineSegment(sketch, "E232", {"start": v(11.29, -21.76) * mm, "end": v(10.98, -17.02) * mm});
            skFitSpline(sketch, "E233", {"points": [v(5, -43.17) * mm, v(4.99, -47.93) * mm, v(4.95, -48.4) * mm, v(4.53, -49.1) * mm]});
            skFitSpline(sketch, "E234", {"points": [v(4.53, -49.1) * mm, v(4.27, -49.52) * mm, v(3.8, -49.96) * mm, v(3.47, -50.08) * mm]});
            skFitSpline(sketch, "E235", {"points": [v(3.47, -50.08) * mm, v(1.93, -50.67) * mm, v(0.16, -50) * mm, v(-0.3, -48.68) * mm]});
            skFitSpline(sketch, "E236", {"points": [v(-0.3, -48.68) * mm, v(-0.47, -48.2) * mm, v(-0.57, -46.02) * mm, v(-0.57, -42.84) * mm]});
            skLineSegment(sketch, "E237", {"start": v(5.7, -37.61) * mm, "end": v(5, -38) * mm});
            skLineSegment(sketch, "E238", {"start": v(5, -38) * mm, "end": v(5, -43.17) * mm});
            skLineSegment(sketch, "E239", {"start": v(5, -43.17) * mm, "end": v(5.7, -37.61) * mm});
            skFitSpline(sketch, "E240", {"points": [v(-1.18, -37.26) * mm, v(-4.05, -34.88) * mm, v(-5.02, -33.39) * mm, v(-5.44, -30.67) * mm]});
            skFitSpline(sketch, "E241", {"points": [v(-5.44, -30.67) * mm, v(-5.81, -28.23) * mm, v(-6.19, -18.27) * mm, v(-5.93, -17.59) * mm]});
            skFitSpline(sketch, "E242", {"points": [v(-5.93, -17.59) * mm, v(-5.62, -16.78) * mm, v(-5.02, -16.47) * mm, v(-3.7, -16.47) * mm]});
            skFitSpline(sketch, "E243", {"points": [v(-3.7, -16.47) * mm, v(-2.89, -16.47) * mm, v(-2.5, -16.6) * mm, v(-2.09, -17.02) * mm]});
            skFitSpline(sketch, "E244", {"points": [v(-2.09, -17.02) * mm, v(-1.42, -17.69) * mm, v(-1.36, -18.15) * mm, v(-1.09, -24.16) * mm]});
            skFitSpline(sketch, "E245", {"points": [v(-1.09, -24.16) * mm, v(-0.89, -28.54) * mm, v(-0.85, -28.78) * mm, v(-0.2, -30.06) * mm]});
            skFitSpline(sketch, "E246", {"points": [v(-0.2, -30.06) * mm, v(0.64, -31.74) * mm, v(1.4, -32.31) * mm, v(2.78, -32.31) * mm]});
            skFitSpline(sketch, "E247", {"points": [v(2.78, -32.31) * mm, v(3.58, -32.31) * mm, v(3.98, -32.17) * mm, v(4.44, -31.75) * mm]});
            skFitSpline(sketch, "E248", {"points": [v(4.44, -31.75) * mm, v(5.86, -30.42) * mm, v(6.24, -28.75) * mm, v(6.5, -22.61) * mm]});
            skFitSpline(sketch, "E249", {"points": [v(6.5, -22.61) * mm, v(6.66, -18.63) * mm, v(6.85, -17.7) * mm, v(7.63, -16.96) * mm]});
            skFitSpline(sketch, "E250", {"points": [v(7.63, -16.96) * mm, v(8.04, -16.57) * mm, v(8.68, -16.39) * mm, v(9.31, -16.4) * mm]});
            skLineSegment(sketch, "E251", {"start": v(-0.57, -42.84) * mm, "end": v(-0.57, -37.76) * mm});
            skLineSegment(sketch, "E252", {"start": v(-0.57, -37.76) * mm, "end": v(-1.18, -37.26) * mm});
            skLineSegment(sketch, "E253", {"start": v(-1.18, -37.26) * mm, "end": v(-0.57, -42.84) * mm});
            skFitSpline(sketch, "E254", {"points": [v(-41.57, -17) * mm, v(-37.32, -16.98) * mm, v(-34.97, -17.8) * mm, v(-33.04, -19.83) * mm]});
            skFitSpline(sketch, "E255", {"points": [v(-33.04, -19.83) * mm, v(-32.16, -20.76) * mm, v(-31.79, -21.4) * mm, v(-31.42, -22.6) * mm]});
            skFitSpline(sketch, "E256", {"points": [v(-31.42, -22.6) * mm, v(-30.96, -24.08) * mm, v(-30.93, -24.7) * mm, v(-30.93, -33.26) * mm]});
            skFitSpline(sketch, "E257", {"points": [v(-30.93, -33.26) * mm, v(-30.93, -39.17) * mm, v(-31.02, -42.82) * mm, v(-31.2, -43.68) * mm]});
            skFitSpline(sketch, "E258", {"points": [v(-31.2, -43.68) * mm, v(-31.74, -46.4) * mm, v(-33.79, -48.62) * mm, v(-36.58, -49.52) * mm]});
            skFitSpline(sketch, "E259", {"points": [v(-36.58, -49.52) * mm, v(-37.97, -49.96) * mm, v(-45.64, -50.2) * mm, v(-46.82, -49.84) * mm]});
            skFitSpline(sketch, "E260", {"points": [v(-46.82, -49.84) * mm, v(-47.2, -49.72) * mm, v(-47.78, -49.35) * mm, v(-48.1, -49.02) * mm]});
            skFitSpline(sketch, "E261", {"points": [v(-48.72, -33.87) * mm, v(-48.77, -24.6) * mm, v(-48.7, -19.1) * mm, v(-48.56, -18.7) * mm]});
            skFitSpline(sketch, "E262", {"points": [v(-48.56, -18.7) * mm, v(-48.11, -17.53) * mm, v(-47.2, -17.23) * mm, v(-43.51, -17.05) * mm]});
            skFitSpline(sketch, "E263", {"points": [v(-43.51, -17.05) * mm, v(-42.82, -17.01) * mm, v(-42.18, -17) * mm, v(-41.57, -17) * mm]});
            skLineSegment(sketch, "E264", {"start": v(-48.1, -49.02) * mm, "end": v(-48.66, -48.42) * mm});
            skLineSegment(sketch, "E265", {"start": v(-48.66, -48.42) * mm, "end": v(-48.72, -33.87) * mm});
            skLineSegment(sketch, "E266", {"start": v(-48.72, -33.87) * mm, "end": v(-48.1, -49.02) * mm});
            skFitSpline(sketch, "E267", {"points": [v(-18.18, -17.29) * mm, v(-16.29, -17.28) * mm, v(-15.8, -17.37) * mm, v(-14.67, -17.9) * mm]});
            skFitSpline(sketch, "E268", {"points": [v(-14.67, -17.9) * mm, v(-12.34, -19) * mm, v(-10.64, -21.22) * mm, v(-10.1, -23.89) * mm]});
            skFitSpline(sketch, "E269", {"points": [v(-10.1, -23.89) * mm, v(-9.66, -26.08) * mm, v(-8.5, -47.03) * mm, v(-8.77, -48.08) * mm]});
            skFitSpline(sketch, "E270", {"points": [v(-8.77, -48.08) * mm, v(-9.04, -49.15) * mm, v(-9.92, -49.85) * mm, v(-11, -49.85) * mm]});
            skFitSpline(sketch, "E271", {"points": [v(-11, -49.85) * mm, v(-12.1, -49.85) * mm, v(-13.19, -49.36) * mm, v(-13.43, -48.75) * mm]});
            skFitSpline(sketch, "E272", {"points": [v(-13.43, -48.75) * mm, v(-13.52, -48.53) * mm, v(-13.74, -47.69) * mm, v(-13.91, -46.89) * mm]});
            skFitSpline(sketch, "E273", {"points": [v(-13.91, -46.89) * mm, v(-14.69, -43.27) * mm, v(-17.68, -41.5) * mm, v(-20.2, -43.17) * mm]});
            skFitSpline(sketch, "E274", {"points": [v(-20.2, -43.17) * mm, v(-21.2, -43.84) * mm, v(-22.36, -45.77) * mm, v(-22.36, -46.8) * mm]});
            skFitSpline(sketch, "E275", {"points": [v(-22.36, -46.8) * mm, v(-22.36, -47.82) * mm, v(-23.24, -49.31) * mm, v(-24.08, -49.7) * mm]});
            skFitSpline(sketch, "E276", {"points": [v(-24.08, -49.7) * mm, v(-25.02, -50.15) * mm, v(-25.27, -50.16) * mm, v(-26.22, -49.74) * mm]});
            skFitSpline(sketch, "E277", {"points": [v(-26.22, -49.74) * mm, v(-27.39, -49.23) * mm, v(-27.77, -48.23) * mm, v(-27.6, -46.15) * mm]});
            skFitSpline(sketch, "E278", {"points": [v(-27.6, -46.15) * mm, v(-25.97, -25.52) * mm, v(-25.78, -23.7) * mm, v(-25.12, -21.93) * mm]});
            skFitSpline(sketch, "E279", {"points": [v(-25.12, -21.93) * mm, v(-24.53, -20.34) * mm, v(-23.08, -18.7) * mm, v(-21.57, -17.91) * mm]});
            skFitSpline(sketch, "E280", {"points": [v(-21.57, -17.91) * mm, v(-20.53, -17.36) * mm, v(-20.13, -17.29) * mm, v(-18.18, -17.29) * mm]});
            skFitSpline(sketch, "E281", {"points": [v(-41.49, -22.28) * mm, v(-42.41, -22.29) * mm, v(-42.93, -22.36) * mm, v(-43.1, -22.5) * mm]});
            skFitSpline(sketch, "E282", {"points": [v(-43.1, -22.5) * mm, v(-43.4, -22.75) * mm, v(-43.45, -24.38) * mm, v(-43.45, -33.61) * mm]});
            skFitSpline(sketch, "E283", {"points": [v(-43.45, -33.61) * mm, v(-43.45, -39.57) * mm, v(-43.38, -44.5) * mm, v(-43.3, -44.6) * mm]});
            skFitSpline(sketch, "E284", {"points": [v(-43.3, -44.6) * mm, v(-43.2, -44.68) * mm, v(-42.05, -44.75) * mm, v(-40.72, -44.75) * mm]});
            skFitSpline(sketch, "E285", {"points": [v(-36.65, -39.68) * mm, v(-36.56, -37.72) * mm, v(-36.56, -33.34) * mm, v(-36.65, -29.96) * mm]});
            skLineSegment(sketch, "E286", {"start": v(-40.72, -44.75) * mm, "end": v(-38.3, -44.75) * mm});
            skLineSegment(sketch, "E287", {"start": v(-38.3, -44.75) * mm, "end": v(-37.55, -44) * mm});
            skLineSegment(sketch, "E288", {"start": v(-37.55, -44) * mm, "end": v(-36.8, -43.24) * mm});
            skLineSegment(sketch, "E289", {"start": v(-36.8, -43.24) * mm, "end": v(-36.65, -39.68) * mm});
            skLineSegment(sketch, "E290", {"start": v(-36.65, -39.68) * mm, "end": v(-40.72, -44.75) * mm});
            skFitSpline(sketch, "E291", {"points": [v(-37.44, -23.1) * mm, v(-38.06, -22.4) * mm, v(-38.14, -22.38) * mm, v(-40.42, -22.3) * mm]});
            skFitSpline(sketch, "E292", {"points": [v(-40.42, -22.3) * mm, v(-40.82, -22.29) * mm, v(-41.18, -22.28) * mm, v(-41.49, -22.28) * mm]});
            skLineSegment(sketch, "E293", {"start": v(-36.65, -29.96) * mm, "end": v(-36.8, -23.81) * mm});
            skLineSegment(sketch, "E294", {"start": v(-36.8, -23.81) * mm, "end": v(-37.44, -23.1) * mm});
            skLineSegment(sketch, "E295", {"start": v(-37.44, -23.1) * mm, "end": v(-36.65, -29.96) * mm});
            skFitSpline(sketch, "E296", {"points": [v(-18, -22.5) * mm, v(-20.27, -22.5) * mm, v(-20.46, -23.01) * mm, v(-21.08, -30.84) * mm]});
            skFitSpline(sketch, "E297", {"points": [v(-21.08, -30.84) * mm, v(-21.36, -34.35) * mm, v(-21.55, -37.28) * mm, v(-21.51, -37.36) * mm]});
            skFitSpline(sketch, "E298", {"points": [v(-21.51, -37.36) * mm, v(-21.47, -37.45) * mm, v(-20.36, -37.46) * mm, v(-19.06, -37.4) * mm]});
            skFitSpline(sketch, "E299", {"points": [v(-19.06, -37.4) * mm, v(-17.67, -37.33) * mm, v(-16.44, -37.39) * mm, v(-16.1, -37.53) * mm]});
            skFitSpline(sketch, "E300", {"points": [v(-16.1, -37.53) * mm, v(-15.78, -37.66) * mm, v(-15.29, -37.77) * mm, v(-15, -37.78) * mm]});
            skFitSpline(sketch, "E301", {"points": [v(-15, -37.78) * mm, v(-14.5, -37.8) * mm, v(-14.48, -37.7) * mm, v(-14.48, -36.23) * mm]});
            skFitSpline(sketch, "E302", {"points": [v(-14.48, -36.23) * mm, v(-14.5, -32.4) * mm, v(-15.13, -24.88) * mm, v(-15.5, -24.18) * mm]});
            skFitSpline(sketch, "E303", {"points": [v(-15.5, -24.18) * mm, v(-16.05, -23.1) * mm, v(-16.95, -22.5) * mm, v(-18, -22.5) * mm]});
            skLineSegment(sketch, "E304", {"start": v(-41.49, -22.28) * mm, "end": v(-41.49, -22.28) * mm});
            skFitSpline(sketch, "E305", {"points": [v(28.1, -59.42) * mm, v(30.53, -59.42) * mm, v(32.39, -60.11) * mm, v(33.67, -61.5) * mm]});
            skFitSpline(sketch, "E306", {"points": [v(33.67, -61.5) * mm, v(34.97, -62.9) * mm, v(35.62, -64.9) * mm, v(35.62, -67.5) * mm]});
            skFitSpline(sketch, "E307", {"points": [v(35.62, -67.5) * mm, v(35.62, -70.48) * mm, v(34.94, -72.77) * mm, v(33.56, -74.38) * mm]});
            skFitSpline(sketch, "E308", {"points": [v(33.56, -74.38) * mm, v(32.19, -75.96) * mm, v(30.22, -76.76) * mm, v(27.65, -76.76) * mm]});
            skFitSpline(sketch, "E309", {"points": [v(27.65, -76.76) * mm, v(26.31, -76.76) * mm, v(24.53, -76.71) * mm, v(22.3, -76.62) * mm]});
            skFitSpline(sketch, "E310", {"points": [v(43.67, -59.42) * mm, v(44.84, -59.42) * mm, v(46.03, -59.69) * mm, v(47.22, -60.22) * mm]});
            skLineSegment(sketch, "E311", {"start": v(22.3, -76.62) * mm, "end": v(22.38, -71.43) * mm});
            skLineSegment(sketch, "E312", {"start": v(22.38, -71.43) * mm, "end": v(22.3, -59.53) * mm});
            skLineSegment(sketch, "E313", {"start": v(22.3, -59.53) * mm, "end": v(28.1, -59.42) * mm});
            skLineSegment(sketch, "E314", {"start": v(28.1, -59.42) * mm, "end": v(22.3, -76.62) * mm});
            skFitSpline(sketch, "E315", {"points": [v(46.72, -61.59) * mm, v(45.68, -60.93) * mm, v(44.61, -60.6) * mm, v(43.5, -60.6) * mm]});
            skFitSpline(sketch, "E316", {"points": [v(43.5, -60.6) * mm, v(42.76, -60.6) * mm, v(42.1, -60.76) * mm, v(41.52, -61.08) * mm]});
            skFitSpline(sketch, "E317", {"points": [v(41.52, -61.08) * mm, v(40.97, -61.38) * mm, v(40.54, -61.78) * mm, v(40.24, -62.28) * mm]});
            skFitSpline(sketch, "E318", {"points": [v(40.24, -62.28) * mm, v(39.96, -62.78) * mm, v(39.81, -63.3) * mm, v(39.81, -63.8) * mm]});
            skFitSpline(sketch, "E319", {"points": [v(39.81, -63.8) * mm, v(39.81, -64.36) * mm, v(39.97, -64.84) * mm, v(40.3, -65.25) * mm]});
            skFitSpline(sketch, "E320", {"points": [v(40.3, -65.25) * mm, v(40.62, -65.66) * mm, v(41, -66.02) * mm, v(41.47, -66.32) * mm]});
            skFitSpline(sketch, "E321", {"points": [v(41.47, -66.32) * mm, v(41.95, -66.6) * mm, v(42.6, -66.94) * mm, v(43.4, -67.31) * mm]});
            skFitSpline(sketch, "E322", {"points": [v(43.4, -67.31) * mm, v(44.34, -67.78) * mm, v(45.1, -68.2) * mm, v(45.67, -68.57) * mm]});
            skFitSpline(sketch, "E323", {"points": [v(45.67, -68.57) * mm, v(46.26, -68.93) * mm, v(46.76, -69.4) * mm, v(47.17, -69.99) * mm]});
            skFitSpline(sketch, "E324", {"points": [v(47.17, -69.99) * mm, v(47.58, -70.56) * mm, v(47.79, -71.25) * mm, v(47.79, -72.08) * mm]});
            skFitSpline(sketch, "E325", {"points": [v(47.79, -72.08) * mm, v(47.79, -72.91) * mm, v(47.55, -73.7) * mm, v(47.1, -74.43) * mm]});
            skFitSpline(sketch, "E326", {"points": [v(47.1, -74.43) * mm, v(46.64, -75.14) * mm, v(46, -75.71) * mm, v(45.16, -76.14) * mm]});
            skFitSpline(sketch, "E327", {"points": [v(45.16, -76.14) * mm, v(44.34, -76.55) * mm, v(43.42, -76.76) * mm, v(42.38, -76.76) * mm]});
            skFitSpline(sketch, "E328", {"points": [v(42.38, -76.76) * mm, v(40.78, -76.76) * mm, v(39.33, -76.36) * mm, v(38.05, -75.55) * mm]});
            skLineSegment(sketch, "E329", {"start": v(47.22, -60.22) * mm, "end": v(46.98, -61.5) * mm});
            skLineSegment(sketch, "E330", {"start": v(46.98, -61.5) * mm, "end": v(46.72, -61.59) * mm});
            skLineSegment(sketch, "E331", {"start": v(46.72, -61.59) * mm, "end": v(47.22, -60.22) * mm});
            skFitSpline(sketch, "E332", {"points": [v(38.4, -74.06) * mm, v(38.98, -74.57) * mm, v(39.64, -74.97) * mm, v(40.37, -75.23) * mm]});
            skFitSpline(sketch, "E333", {"points": [v(40.37, -75.23) * mm, v(41.1, -75.48) * mm, v(41.81, -75.6) * mm, v(42.49, -75.6) * mm]});
            skFitSpline(sketch, "E334", {"points": [v(42.49, -75.6) * mm, v(43.27, -75.6) * mm, v(43.96, -75.45) * mm, v(44.55, -75.13) * mm]});
            skFitSpline(sketch, "E335", {"points": [v(44.55, -75.13) * mm, v(45.14, -74.8) * mm, v(45.6, -74.39) * mm, v(45.91, -73.87) * mm]});
            skFitSpline(sketch, "E336", {"points": [v(45.91, -73.87) * mm, v(46.23, -73.35) * mm, v(46.4, -72.8) * mm, v(46.4, -72.24) * mm]});
            skFitSpline(sketch, "E337", {"points": [v(46.4, -72.24) * mm, v(46.4, -71.65) * mm, v(46.23, -71.14) * mm, v(45.89, -70.71) * mm]});
            skFitSpline(sketch, "E338", {"points": [v(45.89, -70.71) * mm, v(45.57, -70.26) * mm, v(45.16, -69.9) * mm, v(44.68, -69.61) * mm]});
            skFitSpline(sketch, "E339", {"points": [v(44.68, -69.61) * mm, v(44.22, -69.33) * mm, v(43.57, -68.98) * mm, v(42.73, -68.57) * mm]});
            skFitSpline(sketch, "E340", {"points": [v(42.73, -68.57) * mm, v(41.8, -68.12) * mm, v(41.05, -67.72) * mm, v(40.48, -67.37) * mm]});
            skFitSpline(sketch, "E341", {"points": [v(40.48, -67.37) * mm, v(39.91, -67) * mm, v(39.43, -66.55) * mm, v(39.04, -65.97) * mm]});
            skFitSpline(sketch, "E342", {"points": [v(39.04, -65.97) * mm, v(38.64, -65.4) * mm, v(38.45, -64.72) * mm, v(38.45, -63.91) * mm]});
            skFitSpline(sketch, "E343", {"points": [v(38.45, -63.91) * mm, v(38.45, -63.1) * mm, v(38.66, -62.34) * mm, v(39.09, -61.67) * mm]});
            skFitSpline(sketch, "E344", {"points": [v(39.09, -61.67) * mm, v(39.54, -60.97) * mm, v(40.15, -60.43) * mm, v(40.94, -60.03) * mm]});
            skFitSpline(sketch, "E345", {"points": [v(40.94, -60.03) * mm, v(41.74, -59.62) * mm, v(42.65, -59.42) * mm, v(43.67, -59.42) * mm]});
            skLineSegment(sketch, "E346", {"start": v(38.05, -75.55) * mm, "end": v(38.2, -74.14) * mm});
            skLineSegment(sketch, "E347", {"start": v(38.2, -74.14) * mm, "end": v(38.4, -74.06) * mm});
            skLineSegment(sketch, "E348", {"start": v(38.4, -74.06) * mm, "end": v(38.05, -75.55) * mm});
            skFitSpline(sketch, "E349", {"points": [v(12.47, -59.5) * mm, v(14.1, -59.5) * mm, v(15.35, -59.9) * mm, v(16.22, -60.73) * mm]});
            skFitSpline(sketch, "E350", {"points": [v(16.22, -60.73) * mm, v(17.1, -61.55) * mm, v(17.53, -62.74) * mm, v(17.53, -64.29) * mm]});
            skFitSpline(sketch, "E351", {"points": [v(17.53, -64.29) * mm, v(17.53, -65.54) * mm, v(17.21, -66.63) * mm, v(16.57, -67.55) * mm]});
            skFitSpline(sketch, "E352", {"points": [v(16.57, -67.55) * mm, v(15.93, -68.46) * mm, v(15, -69.15) * mm, v(13.81, -69.61) * mm]});
            skFitSpline(sketch, "E353", {"points": [v(13.81, -69.61) * mm, v(15.15, -71.77) * mm, v(16.7, -74) * mm, v(18.44, -76.3) * mm]});
            skFitSpline(sketch, "E354", {"points": [v(18.44, -76.5) * mm, v(18.16, -76.63) * mm, v(17.76, -76.75) * mm, v(17.24, -76.84) * mm]});
            skLineSegment(sketch, "E355", {"start": v(18.44, -76.3) * mm, "end": v(18.44, -76.5) * mm});
            skLineSegment(sketch, "E356", {"start": v(18.44, -76.5) * mm, "end": v(18.44, -76.3) * mm});
            skFitSpline(sketch, "E357", {"points": [v(17.02, -76.73) * mm, v(15.3, -74.25) * mm, v(13.83, -71.99) * mm, v(12.64, -69.93) * mm]});
            skLineSegment(sketch, "E358", {"start": v(17.24, -76.84) * mm, "end": v(17.02, -76.73) * mm});
            skLineSegment(sketch, "E359", {"start": v(17.02, -76.73) * mm, "end": v(17.24, -76.84) * mm});
            skLineSegment(sketch, "E360", {"start": v(12.64, -69.93) * mm, "end": v(9.26, -69.93) * mm});
            skLineSegment(sketch, "E361", {"start": v(9.26, -69.93) * mm, "end": v(9.26, -71.35) * mm});
            skLineSegment(sketch, "E362", {"start": v(9.26, -71.35) * mm, "end": v(9.32, -76.62) * mm});
            skLineSegment(sketch, "E363", {"start": v(9.32, -76.62) * mm, "end": v(7.93, -76.62) * mm});
            skLineSegment(sketch, "E364", {"start": v(7.93, -76.62) * mm, "end": v(8, -71.43) * mm});
            skLineSegment(sketch, "E365", {"start": v(8, -71.43) * mm, "end": v(7.93, -59.53) * mm});
            skLineSegment(sketch, "E366", {"start": v(7.93, -59.53) * mm, "end": v(12.47, -59.5) * mm});
            skLineSegment(sketch, "E367", {"start": v(12.47, -59.5) * mm, "end": v(12.64, -69.93) * mm});
            skLineSegment(sketch, "E368", {"start": v(-40.97, -59.53) * mm, "end": v(-39.39, -59.53) * mm});
            skLineSegment(sketch, "E369", {"start": v(-39.39, -59.53) * mm, "end": v(-33.42, -76.62) * mm});
            skLineSegment(sketch, "E370", {"start": v(-33.42, -76.62) * mm, "end": v(-34.87, -76.62) * mm});
            skLineSegment(sketch, "E371", {"start": v(-34.87, -76.62) * mm, "end": v(-35.24, -75.18) * mm});
            skLineSegment(sketch, "E372", {"start": v(-35.24, -75.18) * mm, "end": v(-36.53, -71.49) * mm});
            skLineSegment(sketch, "E373", {"start": v(-36.53, -71.49) * mm, "end": v(-40.6, -71.43) * mm});
            skLineSegment(sketch, "E374", {"start": v(-40.6, -71.43) * mm, "end": v(-44.26, -71.49) * mm});
            skLineSegment(sketch, "E375", {"start": v(-44.26, -71.49) * mm, "end": v(-45.65, -75.13) * mm});
            skLineSegment(sketch, "E376", {"start": v(-45.65, -75.13) * mm, "end": v(-46.05, -76.62) * mm});
            skLineSegment(sketch, "E377", {"start": v(-46.05, -76.62) * mm, "end": v(-47.5, -76.62) * mm});
            skLineSegment(sketch, "E378", {"start": v(-47.5, -76.62) * mm, "end": v(-40.97, -59.53) * mm});
            skLineSegment(sketch, "E379", {"start": v(-32.65, -59.53) * mm, "end": v(-31.23, -59.53) * mm});
            skLineSegment(sketch, "E380", {"start": v(-31.23, -59.53) * mm, "end": v(-30.91, -60.94) * mm});
            skLineSegment(sketch, "E381", {"start": v(-30.91, -60.94) * mm, "end": v(-26.15, -74.94) * mm});
            skLineSegment(sketch, "E382", {"start": v(-26.15, -74.94) * mm, "end": v(-26.01, -74.94) * mm});
            skLineSegment(sketch, "E383", {"start": v(-26.01, -74.94) * mm, "end": v(-21.92, -63.91) * mm});
            skLineSegment(sketch, "E384", {"start": v(-21.92, -63.91) * mm, "end": v(-23.45, -59.53) * mm});
            skLineSegment(sketch, "E385", {"start": v(-23.45, -59.53) * mm, "end": v(-22, -59.53) * mm});
            skLineSegment(sketch, "E386", {"start": v(-22, -59.53) * mm, "end": v(-21.63, -61.05) * mm});
            skLineSegment(sketch, "E387", {"start": v(-21.63, -61.05) * mm, "end": v(-16.86, -74.94) * mm});
            skLineSegment(sketch, "E388", {"start": v(-16.86, -74.94) * mm, "end": v(-16.7, -74.94) * mm});
            skLineSegment(sketch, "E389", {"start": v(-16.7, -74.94) * mm, "end": v(-11.49, -61) * mm});
            skLineSegment(sketch, "E390", {"start": v(-11.49, -61) * mm, "end": v(-11.11, -59.53) * mm});
            skLineSegment(sketch, "E391", {"start": v(-11.11, -59.53) * mm, "end": v(-9.75, -59.53) * mm});
            skLineSegment(sketch, "E392", {"start": v(-9.75, -59.53) * mm, "end": v(-16.14, -76.62) * mm});
            skLineSegment(sketch, "E393", {"start": v(-16.14, -76.62) * mm, "end": v(-17.56, -76.62) * mm});
            skLineSegment(sketch, "E394", {"start": v(-17.56, -76.62) * mm, "end": v(-21.3, -65.84) * mm});
            skLineSegment(sketch, "E395", {"start": v(-21.3, -65.84) * mm, "end": v(-21.44, -65.84) * mm});
            skLineSegment(sketch, "E396", {"start": v(-21.44, -65.84) * mm, "end": v(-25.45, -76.62) * mm});
            skLineSegment(sketch, "E397", {"start": v(-25.45, -76.62) * mm, "end": v(-26.87, -76.62) * mm});
            skLineSegment(sketch, "E398", {"start": v(-26.87, -76.62) * mm, "end": v(-32.65, -59.53) * mm});
            skFitSpline(sketch, "E399", {"points": [v(28.02, -60.6) * mm, v(26.99, -60.6) * mm, v(25.55, -60.64) * mm, v(23.72, -60.73) * mm]});
            skLineSegment(sketch, "E400", {"start": v(-2.97, -59.53) * mm, "end": v(-1.4, -59.53) * mm});
            skLineSegment(sketch, "E401", {"start": v(-1.4, -59.53) * mm, "end": v(4.57, -76.62) * mm});
            skLineSegment(sketch, "E402", {"start": v(4.57, -76.62) * mm, "end": v(3.13, -76.62) * mm});
            skLineSegment(sketch, "E403", {"start": v(3.13, -76.62) * mm, "end": v(2.75, -75.18) * mm});
            skLineSegment(sketch, "E404", {"start": v(2.75, -75.18) * mm, "end": v(1.47, -71.49) * mm});
            skLineSegment(sketch, "E405", {"start": v(1.47, -71.49) * mm, "end": v(-2.6, -71.43) * mm});
            skLineSegment(sketch, "E406", {"start": v(-2.6, -71.43) * mm, "end": v(-6.27, -71.49) * mm});
            skLineSegment(sketch, "E407", {"start": v(-6.27, -71.49) * mm, "end": v(-7.66, -75.13) * mm});
            skLineSegment(sketch, "E408", {"start": v(-7.66, -75.13) * mm, "end": v(-8.06, -76.62) * mm});
            skLineSegment(sketch, "E409", {"start": v(-8.06, -76.62) * mm, "end": v(-9.5, -76.62) * mm});
            skLineSegment(sketch, "E410", {"start": v(-9.5, -76.62) * mm, "end": v(-2.97, -59.53) * mm});
            skFitSpline(sketch, "E411", {"points": [v(23.69, -75.42) * mm, v(25.33, -75.53) * mm, v(26.71, -75.58) * mm, v(27.84, -75.58) * mm]});
            skFitSpline(sketch, "E412", {"points": [v(27.84, -75.58) * mm, v(29.89, -75.58) * mm, v(31.46, -74.91) * mm, v(32.55, -73.57) * mm]});
            skFitSpline(sketch, "E413", {"points": [v(32.55, -73.57) * mm, v(33.65, -72.24) * mm, v(34.2, -70.3) * mm, v(34.2, -67.74) * mm]});
            skFitSpline(sketch, "E414", {"points": [v(34.2, -67.74) * mm, v(34.2, -65.39) * mm, v(33.68, -63.61) * mm, v(32.63, -62.42) * mm]});
            skFitSpline(sketch, "E415", {"points": [v(32.63, -62.42) * mm, v(31.57, -61.2) * mm, v(30.04, -60.6) * mm, v(28.02, -60.6) * mm]});
            skLineSegment(sketch, "E416", {"start": v(23.72, -60.73) * mm, "end": v(23.64, -71.35) * mm});
            skLineSegment(sketch, "E417", {"start": v(23.64, -71.35) * mm, "end": v(23.69, -75.42) * mm});
            skLineSegment(sketch, "E418", {"start": v(23.69, -75.42) * mm, "end": v(23.72, -60.73) * mm});
            skFitSpline(sketch, "E419", {"points": [v(12.77, -68.76) * mm, v(15, -68.15) * mm, v(16.11, -66.69) * mm, v(16.11, -64.37) * mm]});
            skFitSpline(sketch, "E420", {"points": [v(16.11, -64.37) * mm, v(16.11, -62) * mm, v(14.85, -60.77) * mm, v(12.31, -60.68) * mm]});
            skLineSegment(sketch, "E421", {"start": v(12.31, -60.68) * mm, "end": v(9.34, -60.73) * mm});
            skLineSegment(sketch, "E422", {"start": v(9.34, -60.73) * mm, "end": v(9.3, -68.7) * mm});
            skLineSegment(sketch, "E423", {"start": v(9.3, -68.7) * mm, "end": v(12.77, -68.76) * mm});
            skLineSegment(sketch, "E424", {"start": v(12.77, -68.76) * mm, "end": v(12.31, -60.68) * mm});
            skLineSegment(sketch, "E425", {"start": v(-40.3, -61.13) * mm, "end": v(-43.78, -70.26) * mm});
            skLineSegment(sketch, "E426", {"start": v(-43.78, -70.26) * mm, "end": v(-40.43, -70.28) * mm});
            skLineSegment(sketch, "E427", {"start": v(-40.43, -70.28) * mm, "end": v(-36.95, -70.26) * mm});
            skLineSegment(sketch, "E428", {"start": v(-36.95, -70.26) * mm, "end": v(-40.14, -61.13) * mm});
            skLineSegment(sketch, "E429", {"start": v(-40.14, -61.13) * mm, "end": v(-40.3, -61.13) * mm});
            skLineSegment(sketch, "E430", {"start": v(-2.3, -61.13) * mm, "end": v(-5.78, -70.26) * mm});
            skLineSegment(sketch, "E431", {"start": v(-5.78, -70.26) * mm, "end": v(-2.44, -70.28) * mm});
            skLineSegment(sketch, "E432", {"start": v(-2.44, -70.28) * mm, "end": v(1.04, -70.26) * mm});
            skLineSegment(sketch, "E433", {"start": v(1.04, -70.26) * mm, "end": v(-2.15, -61.13) * mm});
            skLineSegment(sketch, "E434", {"start": v(-2.15, -61.13) * mm, "end": v(-2.3, -61.13) * mm});
            skSolve(sketch);
        }
        {
            var Q0;
            Q0=makeQuery(id+"F0.imprint","IMPRINT",FACE,{"disambiguationData":[TD([[makeQuery(id+"F0.imprint","IMPRINT",EDGE,{"derivedFrom":sQuery(id+"F0.wireOp",EDGE,"E5")}),-1.0]])]});
            var Q1;
            Q1=makeQuery(id+"F0.imprint","IMPRINT",FACE,{"disambiguationData":[TD([[makeQuery(id+"F0.imprint","IMPRINT",EDGE,{"derivedFrom":sQuery(id+"F0.wireOp",EDGE,"E60")}),-1.0]])]});
            var Q2;
            Q2=makeQuery(id+"F0.imprint","IMPRINT",FACE,{"disambiguationData":[TD([[makeQuery(id+"F0.imprint","IMPRINT",EDGE,{"derivedFrom":sQuery(id+"F0.wireOp",EDGE,"E74")}),-1.0]])]});
            var Q3;
            Q3=makeQuery(id+"F0.imprint","IMPRINT",FACE,{"disambiguationData":[TD([[makeQuery(id+"F0.imprint","IMPRINT",EDGE,{"derivedFrom":sQuery(id+"F0.wireOp",EDGE,"E97")}),-1.0]])]});
            var Q4;
            Q4=makeQuery(id+"F0.imprint","IMPRINT",FACE,{"disambiguationData":[TD([[makeQuery(id+"F0.imprint","IMPRINT",EDGE,{"derivedFrom":sQuery(id+"F0.wireOp",EDGE,"E4")}),-1.0]])]});
            var Q5;
            Q5=makeQuery(id+"F0.imprint","IMPRINT",FACE,{"disambiguationData":[TD([[makeQuery(id+"F0.imprint","IMPRINT",EDGE,{"derivedFrom":sQuery(id+"F0.wireOp",EDGE,"E153")}),-1.0]])]});
            var Q6;
            Q6=makeQuery(id+"F0.imprint","IMPRINT",FACE,{"disambiguationData":[TD([[makeQuery(id+"F0.imprint","IMPRINT",EDGE,{"derivedFrom":sQuery(id+"F0.wireOp",EDGE,"E197")}),-1.0]])]});
            var Q7;
            Q7=makeQuery(id+"F0.imprint","IMPRINT",FACE,{"disambiguationData":[TD([[makeQuery(id+"F0.imprint","IMPRINT",EDGE,{"derivedFrom":sQuery(id+"F0.wireOp",EDGE,"E133")}),-1.0]])]});
            var Q8;
            Q8=makeQuery(id+"F0.imprint","IMPRINT",FACE,{"disambiguationData":[TD([[makeQuery(id+"F0.imprint","IMPRINT",EDGE,{"derivedFrom":sQuery(id+"F0.wireOp",EDGE,"E118")}),-1.0]])]});
            var Q9;
            Q9=makeQuery(id+"F0.imprint","IMPRINT",FACE,{"disambiguationData":[TD([[makeQuery(id+"F0.imprint","IMPRINT",EDGE,{"derivedFrom":sQuery(id+"F0.wireOp",EDGE,"E183")}),-1.0]])]});
            var Q10;
            Q10=makeQuery(id+"F0.imprint","IMPRINT",FACE,{"disambiguationData":[TD([[makeQuery(id+"F0.imprint","IMPRINT",EDGE,{"derivedFrom":sQuery(id+"F0.wireOp",EDGE,"E227")}),-1.0]])]});
            var Q11;
            Q11=makeQuery(id+"F0.imprint","IMPRINT",FACE,{"disambiguationData":[TD([[makeQuery(id+"F0.imprint","IMPRINT",EDGE,{"derivedFrom":sQuery(id+"F0.wireOp",EDGE,"E267")}),-1.0]])]});
            var Q12;
            Q12=makeQuery(id+"F0.imprint","IMPRINT",FACE,{"disambiguationData":[TD([[makeQuery(id+"F0.imprint","IMPRINT",EDGE,{"derivedFrom":sQuery(id+"F0.wireOp",EDGE,"E254")}),-1.0]])]});
            extrude(context, id + "F1", {"entities" : qUnion([Q0, Q1, Q2, Q3, Q4, Q5, Q6, Q7, Q8, Q9, Q10, Q11, Q12]), "depth" : 6 * mm});
        }
        {
            var Q0;
            Q0=makeQuery(id+"F0.imprint","IMPRINT",FACE,{"disambiguationData":[TD([[makeQuery(id+"F0.imprint","IMPRINT",EDGE,{"derivedFrom":sQuery(id+"F0.wireOp",EDGE,"E368")}),-1.0]])]});
            var Q1;
            Q1=makeQuery(id+"F0.imprint","IMPRINT",FACE,{"disambiguationData":[TD([[makeQuery(id+"F0.imprint","IMPRINT",EDGE,{"derivedFrom":sQuery(id+"F0.wireOp",EDGE,"E379")}),-1.0]])]});
            var Q2;
            Q2=makeQuery(id+"F0.imprint","IMPRINT",FACE,{"disambiguationData":[TD([[makeQuery(id+"F0.imprint","IMPRINT",EDGE,{"derivedFrom":sQuery(id+"F0.wireOp",EDGE,"E400")}),-1.0]])]});
            var Q3;
            {var subQ1=sQuery(id+"F0.wireOp",EDGE,"E360");Q3=makeQuery(id+"F0.imprint","IMPRINT",FACE,{"disambiguationData":[TD([[makeQuery(id+"F0.imprint","IMPRINT",EDGE,{"derivedFrom":subQ1}),-1.0]])]});}
            var Q4;
            {var subQ5=sQuery(id+"F0.wireOp",EDGE,"E349");Q4=makeQuery(id+"F0.imprint","IMPRINT",FACE,{"disambiguationData":[TD([[makeQuery(id+"F0.imprint","IMPRINT",EDGE,{"derivedFrom":subQ5}),-1.0]])]});}
            var Q5;
            {var subQ7=sQuery(id+"F0.wireOp",EDGE,"E311");Q5=makeQuery(id+"F0.imprint","IMPRINT",FACE,{"disambiguationData":[TD([[makeQuery(id+"F0.imprint","IMPRINT",EDGE,{"derivedFrom":subQ7}),-1.0]])]});}
            var Q6;
            {var subQ4=sQuery(id+"F0.wireOp",EDGE,"E305");Q6=makeQuery(id+"F0.imprint","IMPRINT",FACE,{"disambiguationData":[TD([[makeQuery(id+"F0.imprint","IMPRINT",EDGE,{"derivedFrom":subQ4}),-1.0]])]});}
            var Q7;
            Q7=makeQuery(id+"F0.imprint","IMPRINT",FACE,{"disambiguationData":[TD([[makeQuery(id+"F0.imprint","IMPRINT",EDGE,{"derivedFrom":sQuery(id+"F0.wireOp",EDGE,"E310")}),-1.0]])]});
            extrude(context, id + "F2", {"entities" : qUnion([Q0, Q1, Q2, Q3, Q4, Q5, Q6, Q7]), "depth" : 6 * mm});
        }
        {
            var Q0;
            Q0=makeQuery(id+"F0.imprint","IMPRINT",FACE,{"disambiguationData":[TD([[makeQuery(id+"F0.imprint","IMPRINT",EDGE,{"derivedFrom":sQuery(id+"F0.wireOp",EDGE,"E0")}),1.0]])]});
            var Q1;
            Q1=makeQuery(id+"F0.imprint","IMPRINT",FACE,{"disambiguationData":[TD([[makeQuery(id+"F0.imprint","IMPRINT",EDGE,{"derivedFrom":sQuery(id+"F0.wireOp",EDGE,"E211")}),1.0]])]});
            var Q2;
            Q2=makeQuery(id+"F0.imprint","IMPRINT",FACE,{"disambiguationData":[TD([[makeQuery(id+"F0.imprint","IMPRINT",EDGE,{"derivedFrom":sQuery(id+"F0.wireOp",EDGE,"E281")}),1.0]])]});
            var Q3;
            Q3=makeQuery(id+"F0.imprint","IMPRINT",FACE,{"disambiguationData":[TD([[makeQuery(id+"F0.imprint","IMPRINT",EDGE,{"derivedFrom":sQuery(id+"F0.wireOp",EDGE,"E286")}),1.0]])]});
            var Q4;
            Q4=makeQuery(id+"F0.imprint","IMPRINT",FACE,{"disambiguationData":[TD([[makeQuery(id+"F0.imprint","IMPRINT",EDGE,{"derivedFrom":sQuery(id+"F0.wireOp",EDGE,"E296")}),1.0]])]});
            var Q5;
            Q5=makeQuery(id+"F0.imprint","IMPRINT",FACE,{"disambiguationData":[TD([[makeQuery(id+"F0.imprint","IMPRINT",EDGE,{"derivedFrom":sQuery(id+"F0.wireOp",EDGE,"E150")}),1.0]])]});
            var Q6;
            Q6=makeQuery(id+"F0.imprint","IMPRINT",FACE,{"disambiguationData":[TD([[makeQuery(id+"F0.imprint","IMPRINT",EDGE,{"derivedFrom":sQuery(id+"F0.wireOp",EDGE,"E52")}),1.0]])]});
            var Q7;
            Q7=makeQuery(id+"F0.imprint","IMPRINT",FACE,{"disambiguationData":[TD([[makeQuery(id+"F0.imprint","IMPRINT",EDGE,{"derivedFrom":sQuery(id+"F0.wireOp",EDGE,"E218")}),1.0]])]});
            var Q8;
            Q8=makeQuery(id+"F0.imprint","IMPRINT",FACE,{"disambiguationData":[TD([[makeQuery(id+"F0.imprint","IMPRINT",EDGE,{"derivedFrom":sQuery(id+"F0.wireOp",EDGE,"E425")}),1.0]])]});
            var Q9;
            Q9=makeQuery(id+"F0.imprint","IMPRINT",FACE,{"disambiguationData":[TD([[makeQuery(id+"F0.imprint","IMPRINT",EDGE,{"derivedFrom":sQuery(id+"F0.wireOp",EDGE,"E430")}),1.0]])]});
            var Q10;
            {var subQ4=sQuery(id+"F0.wireOp",EDGE,"E421");Q10=makeQuery(id+"F0.imprint","IMPRINT",FACE,{"disambiguationData":[TD([[makeQuery(id+"F0.imprint","IMPRINT",EDGE,{"derivedFrom":subQ4}),1.0]])]});}
            var Q11;
            {var subQ5=sQuery(id+"F0.wireOp",EDGE,"E419");Q11=makeQuery(id+"F0.imprint","IMPRINT",FACE,{"disambiguationData":[TD([[makeQuery(id+"F0.imprint","IMPRINT",EDGE,{"derivedFrom":subQ5}),1.0]])]});}
            var Q12;
            {var subQ0=sQuery(id+"F0.wireOp",EDGE,"E399");var subQ1=sQuery(id+"F0.wireOp",EDGE,"E314");var subQ2=makeQuery(id+"F0.imprint","INTERSECT",VERTEX,{"derivedFrom":[subQ1,subQ0]});Q12=makeQuery(id+"F0.imprint","IMPRINT",FACE,{"disambiguationData":[TD([[makeQuery(id+"F0.imprint","IMPRINT",EDGE,{"disambiguationData":[TD([[subQ2,-1.0]])],"derivedFrom":subQ1}),-1.0]])]});}
            var Q13;
            {var subQ0=sQuery(id+"F0.wireOp",EDGE,"E411");Q13=makeQuery(id+"F0.imprint","IMPRINT",FACE,{"disambiguationData":[TD([[makeQuery(id+"F0.imprint","IMPRINT",EDGE,{"derivedFrom":subQ0}),1.0]])]});}
            extrude(context, id + "F3", {"entities" : qUnion([Q0, Q1, Q2, Q3, Q4, Q5, Q6, Q7, Q8, Q9, Q10, Q11, Q12, Q13]), "depth" : 6 * mm});
        }
        {
            var Q0;
            Q0=makeQuery(id+"F3.opExtrude","CAP_FACE",FACE,{"disambiguationData":[OSD([sQuery(id+"F0.wireOp",EDGE,"E0"),sQuery(id+"F0.wireOp",EDGE,"E1"),sQuery(id+"F0.wireOp",EDGE,"E2"),sQuery(id+"F0.wireOp",EDGE,"E3"),sQuery(id+"F0.wireOp",EDGE,"E4"),sQuery(id+"F0.wireOp",EDGE,"E5"),sQuery(id+"F0.wireOp",EDGE,"E6"),sQuery(id+"F0.wireOp",EDGE,"E7"),sQuery(id+"F0.wireOp",EDGE,"E8"),sQuery(id+"F0.wireOp",EDGE,"E9"),sQuery(id+"F0.wireOp",EDGE,"E10"),sQuery(id+"F0.wireOp",EDGE,"E11"),sQuery(id+"F0.wireOp",EDGE,"E12"),sQuery(id+"F0.wireOp",EDGE,"E13"),sQuery(id+"F0.wireOp",EDGE,"E14"),sQuery(id+"F0.wireOp",EDGE,"E15"),sQuery(id+"F0.wireOp",EDGE,"E16"),sQuery(id+"F0.wireOp",EDGE,"E17"),sQuery(id+"F0.wireOp",EDGE,"E18"),sQuery(id+"F0.wireOp",EDGE,"E19"),sQuery(id+"F0.wireOp",EDGE,"E20"),sQuery(id+"F0.wireOp",EDGE,"E21"),sQuery(id+"F0.wireOp",EDGE,"E23"),sQuery(id+"F0.wireOp",EDGE,"E24"),sQuery(id+"F0.wireOp",EDGE,"E25"),sQuery(id+"F0.wireOp",EDGE,"E26"),sQuery(id+"F0.wireOp",EDGE,"E27"),sQuery(id+"F0.wireOp",EDGE,"E28"),sQuery(id+"F0.wireOp",EDGE,"E29"),sQuery(id+"F0.wireOp",EDGE,"E31"),sQuery(id+"F0.wireOp",EDGE,"E32"),sQuery(id+"F0.wireOp",EDGE,"E33"),sQuery(id+"F0.wireOp",EDGE,"E34"),sQuery(id+"F0.wireOp",EDGE,"E35"),sQuery(id+"F0.wireOp",EDGE,"E36"),sQuery(id+"F0.wireOp",EDGE,"E38"),sQuery(id+"F0.wireOp",EDGE,"E39"),sQuery(id+"F0.wireOp",EDGE,"E40"),sQuery(id+"F0.wireOp",EDGE,"E41"),sQuery(id+"F0.wireOp",EDGE,"E42"),sQuery(id+"F0.wireOp",EDGE,"E43"),sQuery(id+"F0.wireOp",EDGE,"E44"),sQuery(id+"F0.wireOp",EDGE,"E45"),sQuery(id+"F0.wireOp",EDGE,"E46"),sQuery(id+"F0.wireOp",EDGE,"E49"),sQuery(id+"F0.wireOp",EDGE,"E50"),sQuery(id+"F0.wireOp",EDGE,"E51"),sQuery(id+"F0.wireOp",EDGE,"E52"),sQuery(id+"F0.wireOp",EDGE,"E53"),sQuery(id+"F0.wireOp",EDGE,"E55"),sQuery(id+"F0.wireOp",EDGE,"E56"),sQuery(id+"F0.wireOp",EDGE,"E57"),sQuery(id+"F0.wireOp",EDGE,"E60"),sQuery(id+"F0.wireOp",EDGE,"E61"),sQuery(id+"F0.wireOp",EDGE,"E62"),sQuery(id+"F0.wireOp",EDGE,"E63"),sQuery(id+"F0.wireOp",EDGE,"E64"),sQuery(id+"F0.wireOp",EDGE,"E65"),sQuery(id+"F0.wireOp",EDGE,"E66"),sQuery(id+"F0.wireOp",EDGE,"E67"),sQuery(id+"F0.wireOp",EDGE,"E68"),sQuery(id+"F0.wireOp",EDGE,"E69"),sQuery(id+"F0.wireOp",EDGE,"E70"),sQuery(id+"F0.wireOp",EDGE,"E71"),sQuery(id+"F0.wireOp",EDGE,"E73"),sQuery(id+"F0.wireOp",EDGE,"E74"),sQuery(id+"F0.wireOp",EDGE,"E75"),sQuery(id+"F0.wireOp",EDGE,"E76"),sQuery(id+"F0.wireOp",EDGE,"E77"),sQuery(id+"F0.wireOp",EDGE,"E78"),sQuery(id+"F0.wireOp",EDGE,"E79"),sQuery(id+"F0.wireOp",EDGE,"E80"),sQuery(id+"F0.wireOp",EDGE,"E81"),sQuery(id+"F0.wireOp",EDGE,"E82"),sQuery(id+"F0.wireOp",EDGE,"E83"),sQuery(id+"F0.wireOp",EDGE,"E84"),sQuery(id+"F0.wireOp",EDGE,"E85"),sQuery(id+"F0.wireOp",EDGE,"E86"),sQuery(id+"F0.wireOp",EDGE,"E87"),sQuery(id+"F0.wireOp",EDGE,"E88"),sQuery(id+"F0.wireOp",EDGE,"E89"),sQuery(id+"F0.wireOp",EDGE,"E90"),sQuery(id+"F0.wireOp",EDGE,"E91"),sQuery(id+"F0.wireOp",EDGE,"E92"),sQuery(id+"F0.wireOp",EDGE,"E93"),sQuery(id+"F0.wireOp",EDGE,"E94"),sQuery(id+"F0.wireOp",EDGE,"E96"),sQuery(id+"F0.wireOp",EDGE,"E97"),sQuery(id+"F0.wireOp",EDGE,"E98"),sQuery(id+"F0.wireOp",EDGE,"E99"),sQuery(id+"F0.wireOp",EDGE,"E100"),sQuery(id+"F0.wireOp",EDGE,"E101"),sQuery(id+"F0.wireOp",EDGE,"E102"),sQuery(id+"F0.wireOp",EDGE,"E103"),sQuery(id+"F0.wireOp",EDGE,"E104"),sQuery(id+"F0.wireOp",EDGE,"E105"),sQuery(id+"F0.wireOp",EDGE,"E106"),sQuery(id+"F0.wireOp",EDGE,"E107"),sQuery(id+"F0.wireOp",EDGE,"E108"),sQuery(id+"F0.wireOp",EDGE,"E109"),sQuery(id+"F0.wireOp",EDGE,"E110"),sQuery(id+"F0.wireOp",EDGE,"E111"),sQuery(id+"F0.wireOp",EDGE,"E112"),sQuery(id+"F0.wireOp",EDGE,"E113"),sQuery(id+"F0.wireOp",EDGE,"E114"),sQuery(id+"F0.wireOp",EDGE,"E115"),sQuery(id+"F0.wireOp",EDGE,"E116"),sQuery(id+"F0.wireOp",EDGE,"E118"),sQuery(id+"F0.wireOp",EDGE,"E119"),sQuery(id+"F0.wireOp",EDGE,"E120"),sQuery(id+"F0.wireOp",EDGE,"E121"),sQuery(id+"F0.wireOp",EDGE,"E122"),sQuery(id+"F0.wireOp",EDGE,"E123"),sQuery(id+"F0.wireOp",EDGE,"E124"),sQuery(id+"F0.wireOp",EDGE,"E125"),sQuery(id+"F0.wireOp",EDGE,"E126"),sQuery(id+"F0.wireOp",EDGE,"E127"),sQuery(id+"F0.wireOp",EDGE,"E128"),sQuery(id+"F0.wireOp",EDGE,"E129"),sQuery(id+"F0.wireOp",EDGE,"E130"),sQuery(id+"F0.wireOp",EDGE,"E131"),sQuery(id+"F0.wireOp",EDGE,"E132"),sQuery(id+"F0.wireOp",EDGE,"E133"),sQuery(id+"F0.wireOp",EDGE,"E134"),sQuery(id+"F0.wireOp",EDGE,"E135"),sQuery(id+"F0.wireOp",EDGE,"E136"),sQuery(id+"F0.wireOp",EDGE,"E137"),sQuery(id+"F0.wireOp",EDGE,"E138"),sQuery(id+"F0.wireOp",EDGE,"E139"),sQuery(id+"F0.wireOp",EDGE,"E140"),sQuery(id+"F0.wireOp",EDGE,"E141"),sQuery(id+"F0.wireOp",EDGE,"E142"),sQuery(id+"F0.wireOp",EDGE,"E143"),sQuery(id+"F0.wireOp",EDGE,"E144"),sQuery(id+"F0.wireOp",EDGE,"E145"),sQuery(id+"F0.wireOp",EDGE,"E146"),sQuery(id+"F0.wireOp",EDGE,"E147"),sQuery(id+"F0.wireOp",EDGE,"E148"),sQuery(id+"F0.wireOp",EDGE,"E149"),sQuery(id+"F0.wireOp",EDGE,"E150"),sQuery(id+"F0.wireOp",EDGE,"E151"),sQuery(id+"F0.wireOp",EDGE,"E153"),sQuery(id+"F0.wireOp",EDGE,"E154"),sQuery(id+"F0.wireOp",EDGE,"E155"),sQuery(id+"F0.wireOp",EDGE,"E157"),sQuery(id+"F0.wireOp",EDGE,"E158"),sQuery(id+"F0.wireOp",EDGE,"E159"),sQuery(id+"F0.wireOp",EDGE,"E162"),sQuery(id+"F0.wireOp",EDGE,"E163"),sQuery(id+"F0.wireOp",EDGE,"E164"),sQuery(id+"F0.wireOp",EDGE,"E165"),sQuery(id+"F0.wireOp",EDGE,"E166"),sQuery(id+"F0.wireOp",EDGE,"E167"),sQuery(id+"F0.wireOp",EDGE,"E168"),sQuery(id+"F0.wireOp",EDGE,"E169"),sQuery(id+"F0.wireOp",EDGE,"E170"),sQuery(id+"F0.wireOp",EDGE,"E171"),sQuery(id+"F0.wireOp",EDGE,"E172"),sQuery(id+"F0.wireOp",EDGE,"E173"),sQuery(id+"F0.wireOp",EDGE,"E174"),sQuery(id+"F0.wireOp",EDGE,"E175"),sQuery(id+"F0.wireOp",EDGE,"E176"),sQuery(id+"F0.wireOp",EDGE,"E177"),sQuery(id+"F0.wireOp",EDGE,"E178"),sQuery(id+"F0.wireOp",EDGE,"E179"),sQuery(id+"F0.wireOp",EDGE,"E180"),sQuery(id+"F0.wireOp",EDGE,"E181"),sQuery(id+"F0.wireOp",EDGE,"E183"),sQuery(id+"F0.wireOp",EDGE,"E184"),sQuery(id+"F0.wireOp",EDGE,"E185"),sQuery(id+"F0.wireOp",EDGE,"E186"),sQuery(id+"F0.wireOp",EDGE,"E187"),sQuery(id+"F0.wireOp",EDGE,"E188"),sQuery(id+"F0.wireOp",EDGE,"E189"),sQuery(id+"F0.wireOp",EDGE,"E190"),sQuery(id+"F0.wireOp",EDGE,"E191"),sQuery(id+"F0.wireOp",EDGE,"E192"),sQuery(id+"F0.wireOp",EDGE,"E193"),sQuery(id+"F0.wireOp",EDGE,"E194"),sQuery(id+"F0.wireOp",EDGE,"E195"),sQuery(id+"F0.wireOp",EDGE,"E197"),sQuery(id+"F0.wireOp",EDGE,"E198"),sQuery(id+"F0.wireOp",EDGE,"E199"),sQuery(id+"F0.wireOp",EDGE,"E200"),sQuery(id+"F0.wireOp",EDGE,"E201"),sQuery(id+"F0.wireOp",EDGE,"E202"),sQuery(id+"F0.wireOp",EDGE,"E203"),sQuery(id+"F0.wireOp",EDGE,"E204"),sQuery(id+"F0.wireOp",EDGE,"E205"),sQuery(id+"F0.wireOp",EDGE,"E206"),sQuery(id+"F0.wireOp",EDGE,"E207"),sQuery(id+"F0.wireOp",EDGE,"E208"),sQuery(id+"F0.wireOp",EDGE,"E209"),sQuery(id+"F0.wireOp",EDGE,"E210"),sQuery(id+"F0.wireOp",EDGE,"E227"),sQuery(id+"F0.wireOp",EDGE,"E228"),sQuery(id+"F0.wireOp",EDGE,"E229"),sQuery(id+"F0.wireOp",EDGE,"E230"),sQuery(id+"F0.wireOp",EDGE,"E231"),sQuery(id+"F0.wireOp",EDGE,"E233"),sQuery(id+"F0.wireOp",EDGE,"E234"),sQuery(id+"F0.wireOp",EDGE,"E235"),sQuery(id+"F0.wireOp",EDGE,"E236"),sQuery(id+"F0.wireOp",EDGE,"E239"),sQuery(id+"F0.wireOp",EDGE,"E240"),sQuery(id+"F0.wireOp",EDGE,"E241"),sQuery(id+"F0.wireOp",EDGE,"E242"),sQuery(id+"F0.wireOp",EDGE,"E243"),sQuery(id+"F0.wireOp",EDGE,"E244"),sQuery(id+"F0.wireOp",EDGE,"E245"),sQuery(id+"F0.wireOp",EDGE,"E246"),sQuery(id+"F0.wireOp",EDGE,"E247"),sQuery(id+"F0.wireOp",EDGE,"E248"),sQuery(id+"F0.wireOp",EDGE,"E249"),sQuery(id+"F0.wireOp",EDGE,"E250"),sQuery(id+"F0.wireOp",EDGE,"E253"),sQuery(id+"F0.wireOp",EDGE,"E254"),sQuery(id+"F0.wireOp",EDGE,"E255"),sQuery(id+"F0.wireOp",EDGE,"E256"),sQuery(id+"F0.wireOp",EDGE,"E257"),sQuery(id+"F0.wireOp",EDGE,"E258"),sQuery(id+"F0.wireOp",EDGE,"E259"),sQuery(id+"F0.wireOp",EDGE,"E260"),sQuery(id+"F0.wireOp",EDGE,"E261"),sQuery(id+"F0.wireOp",EDGE,"E262"),sQuery(id+"F0.wireOp",EDGE,"E263"),sQuery(id+"F0.wireOp",EDGE,"E264"),sQuery(id+"F0.wireOp",EDGE,"E265"),sQuery(id+"F0.wireOp",EDGE,"E267"),sQuery(id+"F0.wireOp",EDGE,"E268"),sQuery(id+"F0.wireOp",EDGE,"E269"),sQuery(id+"F0.wireOp",EDGE,"E270"),sQuery(id+"F0.wireOp",EDGE,"E271"),sQuery(id+"F0.wireOp",EDGE,"E272"),sQuery(id+"F0.wireOp",EDGE,"E273"),sQuery(id+"F0.wireOp",EDGE,"E274"),sQuery(id+"F0.wireOp",EDGE,"E275"),sQuery(id+"F0.wireOp",EDGE,"E276"),sQuery(id+"F0.wireOp",EDGE,"E277"),sQuery(id+"F0.wireOp",EDGE,"E278"),sQuery(id+"F0.wireOp",EDGE,"E279"),sQuery(id+"F0.wireOp",EDGE,"E280"),sQuery(id+"F0.wireOp",EDGE,"E305"),sQuery(id+"F0.wireOp",EDGE,"E306"),sQuery(id+"F0.wireOp",EDGE,"E307"),sQuery(id+"F0.wireOp",EDGE,"E308"),sQuery(id+"F0.wireOp",EDGE,"E309"),sQuery(id+"F0.wireOp",EDGE,"E310"),sQuery(id+"F0.wireOp",EDGE,"E311"),sQuery(id+"F0.wireOp",EDGE,"E312"),sQuery(id+"F0.wireOp",EDGE,"E313"),sQuery(id+"F0.wireOp",EDGE,"E315"),sQuery(id+"F0.wireOp",EDGE,"E316"),sQuery(id+"F0.wireOp",EDGE,"E317"),sQuery(id+"F0.wireOp",EDGE,"E318"),sQuery(id+"F0.wireOp",EDGE,"E319"),sQuery(id+"F0.wireOp",EDGE,"E320"),sQuery(id+"F0.wireOp",EDGE,"E321"),sQuery(id+"F0.wireOp",EDGE,"E322"),sQuery(id+"F0.wireOp",EDGE,"E323"),sQuery(id+"F0.wireOp",EDGE,"E324"),sQuery(id+"F0.wireOp",EDGE,"E325"),sQuery(id+"F0.wireOp",EDGE,"E326"),sQuery(id+"F0.wireOp",EDGE,"E327"),sQuery(id+"F0.wireOp",EDGE,"E328"),sQuery(id+"F0.wireOp",EDGE,"E329"),sQuery(id+"F0.wireOp",EDGE,"E330"),sQuery(id+"F0.wireOp",EDGE,"E332"),sQuery(id+"F0.wireOp",EDGE,"E333"),sQuery(id+"F0.wireOp",EDGE,"E334"),sQuery(id+"F0.wireOp",EDGE,"E335"),sQuery(id+"F0.wireOp",EDGE,"E336"),sQuery(id+"F0.wireOp",EDGE,"E337"),sQuery(id+"F0.wireOp",EDGE,"E338"),sQuery(id+"F0.wireOp",EDGE,"E339"),sQuery(id+"F0.wireOp",EDGE,"E340"),sQuery(id+"F0.wireOp",EDGE,"E341"),sQuery(id+"F0.wireOp",EDGE,"E342"),sQuery(id+"F0.wireOp",EDGE,"E343"),sQuery(id+"F0.wireOp",EDGE,"E344"),sQuery(id+"F0.wireOp",EDGE,"E345"),sQuery(id+"F0.wireOp",EDGE,"E346"),sQuery(id+"F0.wireOp",EDGE,"E347"),sQuery(id+"F0.wireOp",EDGE,"E349"),sQuery(id+"F0.wireOp",EDGE,"E350"),sQuery(id+"F0.wireOp",EDGE,"E351"),sQuery(id+"F0.wireOp",EDGE,"E352"),sQuery(id+"F0.wireOp",EDGE,"E353"),sQuery(id+"F0.wireOp",EDGE,"E354"),sQuery(id+"F0.wireOp",EDGE,"E356"),sQuery(id+"F0.wireOp",EDGE,"E357"),sQuery(id+"F0.wireOp",EDGE,"E359"),sQuery(id+"F0.wireOp",EDGE,"E360"),sQuery(id+"F0.wireOp",EDGE,"E361"),sQuery(id+"F0.wireOp",EDGE,"E362"),sQuery(id+"F0.wireOp",EDGE,"E363"),sQuery(id+"F0.wireOp",EDGE,"E364"),sQuery(id+"F0.wireOp",EDGE,"E365"),sQuery(id+"F0.wireOp",EDGE,"E366"),sQuery(id+"F0.wireOp",EDGE,"E368"),sQuery(id+"F0.wireOp",EDGE,"E369"),sQuery(id+"F0.wireOp",EDGE,"E370"),sQuery(id+"F0.wireOp",EDGE,"E371"),sQuery(id+"F0.wireOp",EDGE,"E372"),sQuery(id+"F0.wireOp",EDGE,"E373"),sQuery(id+"F0.wireOp",EDGE,"E374"),sQuery(id+"F0.wireOp",EDGE,"E375"),sQuery(id+"F0.wireOp",EDGE,"E376"),sQuery(id+"F0.wireOp",EDGE,"E377"),sQuery(id+"F0.wireOp",EDGE,"E378"),sQuery(id+"F0.wireOp",EDGE,"E379"),sQuery(id+"F0.wireOp",EDGE,"E380"),sQuery(id+"F0.wireOp",EDGE,"E381"),sQuery(id+"F0.wireOp",EDGE,"E382"),sQuery(id+"F0.wireOp",EDGE,"E383"),sQuery(id+"F0.wireOp",EDGE,"E384"),sQuery(id+"F0.wireOp",EDGE,"E385"),sQuery(id+"F0.wireOp",EDGE,"E386"),sQuery(id+"F0.wireOp",EDGE,"E387"),sQuery(id+"F0.wireOp",EDGE,"E388"),sQuery(id+"F0.wireOp",EDGE,"E389"),sQuery(id+"F0.wireOp",EDGE,"E390"),sQuery(id+"F0.wireOp",EDGE,"E391"),sQuery(id+"F0.wireOp",EDGE,"E392"),sQuery(id+"F0.wireOp",EDGE,"E393"),sQuery(id+"F0.wireOp",EDGE,"E394"),sQuery(id+"F0.wireOp",EDGE,"E395"),sQuery(id+"F0.wireOp",EDGE,"E396"),sQuery(id+"F0.wireOp",EDGE,"E397"),sQuery(id+"F0.wireOp",EDGE,"E398"),sQuery(id+"F0.wireOp",EDGE,"E400"),sQuery(id+"F0.wireOp",EDGE,"E401"),sQuery(id+"F0.wireOp",EDGE,"E402"),sQuery(id+"F0.wireOp",EDGE,"E403"),sQuery(id+"F0.wireOp",EDGE,"E404"),sQuery(id+"F0.wireOp",EDGE,"E405"),sQuery(id+"F0.wireOp",EDGE,"E406"),sQuery(id+"F0.wireOp",EDGE,"E407"),sQuery(id+"F0.wireOp",EDGE,"E408"),sQuery(id+"F0.wireOp",EDGE,"E409"),sQuery(id+"F0.wireOp",EDGE,"E410")])],"isStart":false});
            var sketch = newSketch(context, id + "F4", { "sketchPlane" : qUnion([Q0])});
            skLineSegment(sketch, "E435", {"start": v(-194.17, -122.58) * mm, "end": v(70.56, -122.58) * mm});
            skLineSegment(sketch, "E436", {"start": v(-194.17, -122.58) * mm, "end": v(-194.17, -62.37) * mm});
            skSolve(sketch);
        }
        {
            var Q0;
            Q0=makeQuery(id+"F4.imprint","IMPRINT",FACE,{"disambiguationData":[TD([[makeQuery(id+"F4.imprint","IMPRINT",EDGE,{"derivedFrom":sQuery(id+"F4.wireOp",EDGE,"E435")}),1.0]])]});
            extrude(context, id + "F5", {"entities" : qUnion([Q0]), "oppositeDirection" : true, "depth" : 6 * mm});
        }
    });
